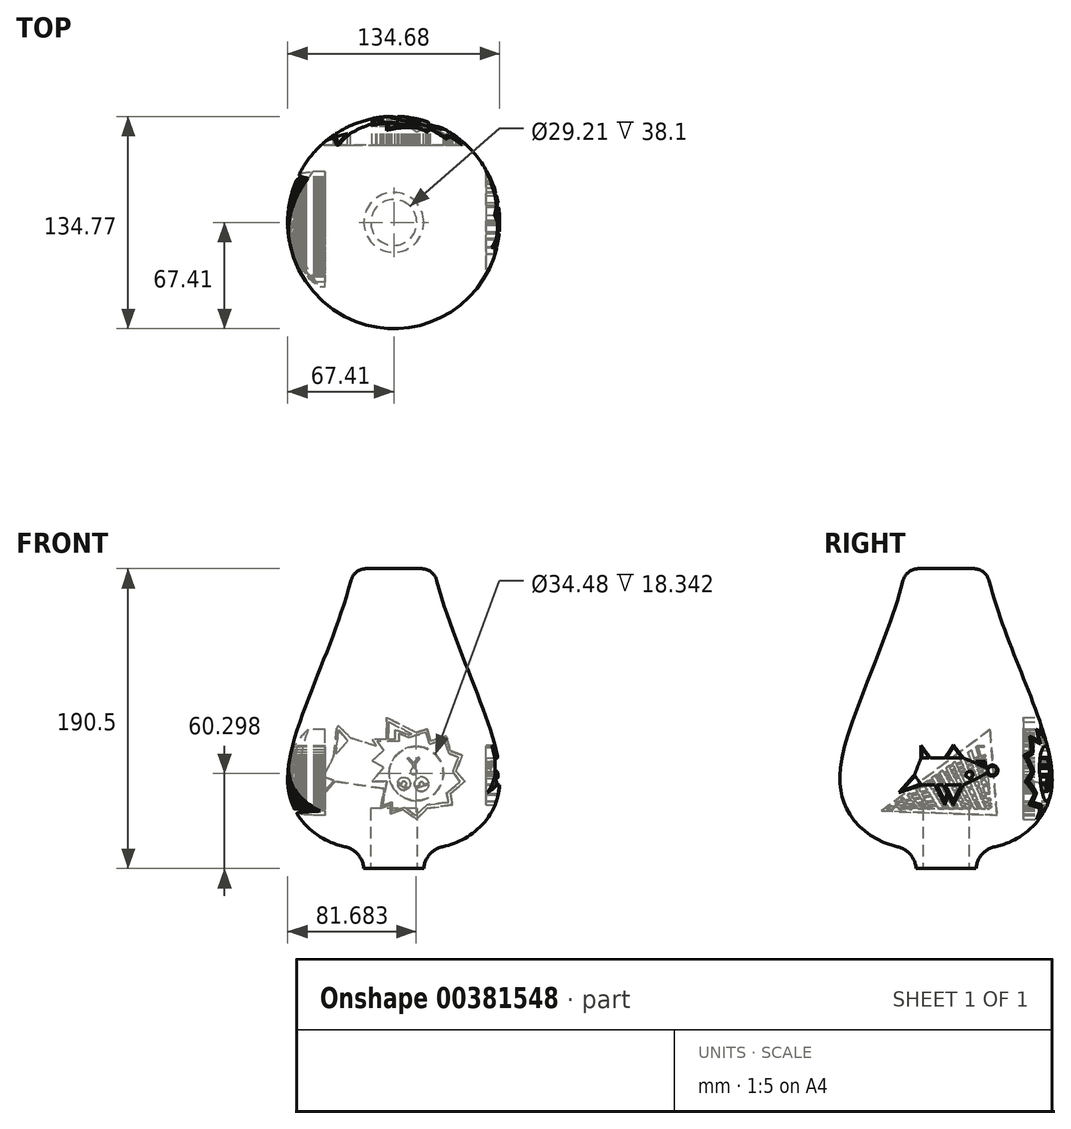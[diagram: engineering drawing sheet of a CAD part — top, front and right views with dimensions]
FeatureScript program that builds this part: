
annotation { "Feature Type Name" : "Feature", "Feature Type Description" : "" }
export const myFeature = defineFeature(function(context is Context, id is Id, definition is map)
    precondition{}
    {
        {
            var Q0;
            Q0=qCreatedBy(makeId("Right.planeOp"),FACE);
            var sketch = newSketch(context, id + "F0", { "sketchPlane" : qUnion([Q0])});
            skLineSegment(sketch, "E0", {"start": v(0, 38.68) * mm, "end": v(0, -139.12) * mm});
            skLineSegment(sketch, "E1", {"start": v(0, 38.68) * mm, "end": v(-25.4, 38.68) * mm});
            skFitSpline(sketch, "E2", {"points": [v(0, -139.12) * mm, v(-39.73, -135.25) * mm, v(-67.26, -98.84) * mm, v(-25.4, 38.68) * mm], "startDerivative": vector(-163.88, -7.65) * mm, "endDerivative": vector(75.35, 332.23) * mm});
            skLineSegment(sketch, "E3", {"start": v(0, -139.12) * mm, "end": v(-21.65, -139.3) * mm});
            skPoint(sketch, "E4.orphan", {"position": v(-79.02, -139.76) * mm});
            skSolve(sketch);
        }
        {
            var Q0;
            Q0=makeQuery(id+"F0.imprint","IMPRINT",FACE,{"disambiguationData":[TD([[makeQuery(id+"F0.imprint","IMPRINT",EDGE,{"derivedFrom":sQuery(id+"F0.wireOp",EDGE,"E0")}),-1.0]])]});
            var Q1;
            Q1=sQuery(id+"F0.wireOp",EDGE,"E0");
            revolve(context, id + "F1", {"entities" : qUnion([Q0]), "axis" : qUnion([Q1]), "revolveType" : RevolveType.FULL});
        }
        {
            var Q0;
            Q0=makeQuery(id+"F1.opRevolve","SWEPT_FACE",FACE,{"disambiguationData":[OSD([sQuery(id+"F0.wireOp",EDGE,"E1")])]});
            cPlane(context, id + "F2", {"entities" : qUnion([Q0]), "cplaneType" : CPlaneType.OFFSET, "offset" : 177.8 * mm, "oppositeDirection" : true, "width" : 152.4 * mm, "height" : 152.4 * mm});
        }
        {
            var Q0;
            Q0=qCreatedBy(id+"F2.planeOp",FACE);
            var sketch = newSketch(context, id + "F3", { "sketchPlane" : qUnion([Q0])});
            skCircle(sketch, "E5", {"center": v(0, 0) * mm, "radius": 19.05 * mm});
            skCircle(sketch, "E6", {"center": v(0, 0) * mm, "radius": 14.6 * mm});
            skSolve(sketch);
        }
        {
            var Q0;
            Q0=makeQuery(id+"F3.imprint","IMPRINT",FACE,{"disambiguationData":[TD([[makeQuery(id+"F3.imprint","IMPRINT",EDGE,{"derivedFrom":sQuery(id+"F3.wireOp",EDGE,"E6")}),1.0]])]});
            extrude(context, id + "F4", {"entities" : qUnion([Q0]), "operationType" : NewBodyOperationType.REMOVE, "depth" : 25.4 * mm, "hasSecondDirection" : true, "secondDirectionOppositeDirection" : true, "secondDirectionDepth" : 121.16 * mm});
        }
        {
            var Q0;
            Q0=qCreatedBy(makeId("Right.planeOp"),FACE);
            cPlane(context, id + "F5", {"entities" : qUnion([Q0]), "cplaneType" : CPlaneType.OFFSET, "offset" : 69.1 * mm, "width" : 152.4 * mm, "height" : 152.4 * mm});
        }
        {
            var Q0;
            Q0 = qSketchRegion(id + "F3", true);
            extrude(context, id + "F6", {"entities" : qUnion([Q0]), "operationType" : NewBodyOperationType.ADD, "oppositeDirection" : true, "depth" : 12.7 * mm});
        }
        {
            var Q0;
            Q0=makeQuery(id+"F6.boolean.opBoolean","INTERSECT",EDGE,{"derivedFrom":[makeQuery(id+"F1.opRevolve","SWEPT_FACE",FACE,{"disambiguationData":[OSD([sQuery(id+"F0.wireOp",EDGE,"E3")])]}),makeQuery(id+"F6.opExtrude","SWEPT_FACE",FACE,{"disambiguationData":[OSD([sQuery(id+"F3.wireOp",EDGE,"E5")])]})]});
            fillet(context, id + "F7", {"entities" : qUnion([Q0]), "radius" : 15.24 * mm, "tangentPropagation" : true, "allowEdgeOverflow" : false});
        }
        {
            var Q0;
            Q0=makeQuery(id+"F1.opRevolve","SWEPT_EDGE",EDGE,{"disambiguationData":[OSD([sQuery(id+"F0.wireOp",EDGE,"E1"),sQuery(id+"F0.wireOp",EDGE,"E2")])]});
            fillet(context, id + "F8", {"entities" : qUnion([Q0]), "radius" : 10.16 * mm, "tangentPropagation" : true, "allowEdgeOverflow" : false});
        }
        {
            var Q0;
            Q0=qCreatedBy(id+"F5.planeOp",FACE);
            var sketch = newSketch(context, id + "F9", { "sketchPlane" : qUnion([Q0])});
            skPoint(sketch, "E7.endSnap0", {"position": v(0.02, -69.9) * mm});
            skPoint(sketch, "E8.endSnap0", {"position": v(4.6, -119.36) * mm});
            skLineSegment(sketch, "E9", {"start": v(10.93, -98.82) * mm, "end": v(4.58, -111.52) * mm});
            skLineSegment(sketch, "E10", {"start": v(4.58, -111.52) * mm, "end": v(1.4, -105.17) * mm});
            skLineSegment(sketch, "E11", {"start": v(-15.48, -98.82) * mm, "end": v(-7.06, -98.82) * mm});
            skLineSegment(sketch, "E12", {"start": v(10.93, -98.82) * mm, "end": v(26.8, -90.88) * mm});
            skLineSegment(sketch, "E13", {"start": v(26.75, -88.46) * mm, "end": v(22.07, -86.39) * mm});
            skLineSegment(sketch, "E14", {"start": v(10.93, -81.45) * mm, "end": v(4.58, -73.28) * mm});
            skLineSegment(sketch, "E15", {"start": v(4.58, -73.28) * mm, "end": v(-0.66, -81.45) * mm});
            skLineSegment(sketch, "E16", {"start": v(-0.66, -81.45) * mm, "end": v(-10.09, -81.45) * mm});
            skLineSegment(sketch, "E17", {"start": v(-10.09, -81.45) * mm, "end": v(-15.9, -73.59) * mm});
            skLineSegment(sketch, "E18", {"start": v(-15.9, -73.59) * mm, "end": v(-15.9, -81.45) * mm});
            skArc(sketch, "E19", {"start": v(26.8, -90.88) * mm, "mid": v(32.19, -89.55) * mm, "end": v(26.75, -88.46) * mm});
            skPoint(sketch, "E20.start.orphan", {"position": v(-9.13, -111.52) * mm});
            skLineSegment(sketch, "E21", {"start": v(1.4, -105.17) * mm, "end": v(-0.82, -111.3) * mm});
            skLineSegment(sketch, "E22", {"start": v(-0.82, -111.3) * mm, "end": v(-7.06, -98.82) * mm});
            skLineSegment(sketch, "E23", {"start": v(-15.9, -81.45) * mm, "end": v(-20.1, -92.38) * mm});
            skLineSegment(sketch, "E24", {"start": v(-20.1, -92.38) * mm, "end": v(-29.9, -103.5) * mm});
            skLineSegment(sketch, "E25", {"start": v(-29.9, -103.5) * mm, "end": v(-15.48, -98.82) * mm});
            skCircle(sketch, "E26", {"center": v(14.89, -92.23) * mm, "radius": 2.23 * mm});
            skLineSegment(sketch, "E27", {"start": v(24.42, -87.42) * mm, "end": v(24.42, -84.23) * mm});
            skLineSegment(sketch, "E28", {"start": v(24.42, -84.23) * mm, "end": v(22.07, -84.23) * mm});
            skLineSegment(sketch, "E29", {"start": v(21.78, -84.23) * mm, "end": v(21.78, -86.25) * mm});
            skLineSegment(sketch, "E30", {"start": v(21.78, -84.23) * mm, "end": v(19.44, -84.23) * mm});
            skLineSegment(sketch, "E31", {"start": v(19.44, -84.23) * mm, "end": v(19.44, -85.22) * mm});
            skCircle(sketch, "E32", {"center": v(29.35, -89.61) * mm, "radius": 2.84 * mm});
            skLineSegment(sketch, "E33", {"start": v(25.01, -87.69) * mm, "end": v(25.01, -83.8) * mm});
            skLineSegment(sketch, "E34", {"start": v(25.01, -83.8) * mm, "end": v(18.9, -83.8) * mm});
            skLineSegment(sketch, "E35", {"start": v(18.9, -83.8) * mm, "end": v(18.9, -84.97) * mm});
            skArc(sketch, "E36", {"start": v(26.2, -91.19) * mm, "mid": v(32.88, -89.53) * mm, "end": v(26.12, -88.18) * mm});
            skLineSegment(sketch, "E37", {"start": v(22.07, -84.23) * mm, "end": v(22.07, -86.39) * mm});
            skLineSegment(sketch, "E38.trimOffspring", {"start": v(21.78, -86.25) * mm, "end": v(10.93, -81.45) * mm});
            skLineSegment(sketch, "E39", {"start": v(9.83, -98.82) * mm, "end": v(-0.82, -98.82) * mm});
            skLineSegment(sketch, "E40", {"start": v(9.83, -98.82) * mm, "end": v(4.58, -109.32) * mm});
            skLineSegment(sketch, "E41", {"start": v(4.58, -109.32) * mm, "end": v(-0.82, -98.82) * mm});
            skLineSegment(sketch, "E42", {"start": v(-5.86, -98.82) * mm, "end": v(-0.82, -108.9) * mm});
            skLineSegment(sketch, "E43", {"start": v(-0.82, -108.9) * mm, "end": v(0.9, -104.16) * mm});
            skLineSegment(sketch, "E44.trimOffspring", {"start": v(0.9, -104.16) * mm, "end": v(-1.77, -98.82) * mm});
            skLineSegment(sketch, "E45.trimOffspring", {"start": v(-1.77, -98.82) * mm, "end": v(-5.86, -98.82) * mm});
            skLineSegment(sketch, "E46", {"start": v(10.27, -81.45) * mm, "end": v(4.58, -81.45) * mm});
            skLineSegment(sketch, "E47", {"start": v(10.27, -81.45) * mm, "end": v(4.58, -74.19) * mm});
            skPoint(sketch, "E48.end.orphan", {"position": v(4.58, -81.45) * mm});
            skLineSegment(sketch, "E49", {"start": v(-10.85, -81.45) * mm, "end": v(-15.45, -81.45) * mm});
            skLineSegment(sketch, "E50", {"start": v(-10.85, -81.45) * mm, "end": v(-15.45, -74.88) * mm});
            skLineSegment(sketch, "E51", {"start": v(-15.45, -74.88) * mm, "end": v(-15.45, -81.45) * mm});
            skLineSegment(sketch, "E52", {"start": v(10.27, -81.45) * mm, "end": v(-0.08, -81.45) * mm});
            skLineSegment(sketch, "E53", {"start": v(4.58, -74.19) * mm, "end": v(-0.08, -81.45) * mm});
            skPoint(sketch, "E54.orphan", {"position": v(-0.22, -81.45) * mm});
            skLineSegment(sketch, "E55", {"start": v(-15.92, -98.2) * mm, "end": v(-19.67, -92.97) * mm});
            skLineSegment(sketch, "E56", {"start": v(-17.79, -95.6) * mm, "end": v(-15.92, -98.2) * mm});
            skLineSegment(sketch, "E57", {"start": v(-15.92, -98.2) * mm, "end": v(-28.98, -102.9) * mm});
            skLineSegment(sketch, "E58", {"start": v(-28.98, -102.9) * mm, "end": v(-19.67, -92.97) * mm});
            skSolve(sketch);
        }
        {
            var Q0;
            {var subQ7=sQuery(id+"F9.wireOp",EDGE,"E9");Q0=makeQuery(id+"F9.imprint","IMPRINT",FACE,{"disambiguationData":[TD([[makeQuery(id+"F9.imprint","IMPRINT",EDGE,{"derivedFrom":subQ7}),-1.0]])]});}
            var Q1;
            {var subQ3=sQuery(id+"F9.wireOp",EDGE,"E36");Q1=makeQuery(id+"F9.imprint","IMPRINT",FACE,{"disambiguationData":[TD([[makeQuery(id+"F9.imprint","IMPRINT",EDGE,{"derivedFrom":subQ3}),1.0]])]});}
            var Q2;
            {var subQ0=sQuery(id+"F9.wireOp",EDGE,"E27");Q2=makeQuery(id+"F9.imprint","IMPRINT",FACE,{"disambiguationData":[TD([[makeQuery(id+"F9.imprint","IMPRINT",EDGE,{"derivedFrom":subQ0}),-1.0]])]});}
            extrude(context, id + "F10", {"entities" : qUnion([Q0, Q1, Q2]), "operationType" : NewBodyOperationType.REMOVE, "oppositeDirection" : true, "depth" : 10.67 * mm});
        }
        {
            var Q0;
            Q0=qCreatedBy(makeId("Front.planeOp"),FACE);
            cPlane(context, id + "F11", {"entities" : qUnion([Q0]), "cplaneType" : CPlaneType.OFFSET, "offset" : 69.1 * mm, "oppositeDirection" : true, "width" : 152.4 * mm, "height" : 152.4 * mm});
        }
        {
            var Q0;
            Q0=qCreatedBy(id+"F11.planeOp",FACE);
            var sketch = newSketch(context, id + "F12", { "sketchPlane" : qUnion([Q0])});
            skCircle(sketch, "E59", {"center": v(14.27, -91.52) * mm, "radius": 17.24 * mm});
            skLineSegment(sketch, "E60", {"start": v(5.73, -114.4) * mm, "end": v(14.47, -120.5) * mm});
            skLineSegment(sketch, "E61", {"start": v(14.47, -120.5) * mm, "end": v(21.2, -113.75) * mm});
            skLineSegment(sketch, "E62", {"start": v(21.2, -113.75) * mm, "end": v(37.14, -111.33) * mm});
            skLineSegment(sketch, "E63", {"start": v(37.14, -111.33) * mm, "end": v(36.07, -104.25) * mm});
            skLineSegment(sketch, "E64", {"start": v(36.07, -104.25) * mm, "end": v(45.1, -96.63) * mm});
            skLineSegment(sketch, "E65", {"start": v(45.1, -96.63) * mm, "end": v(39.67, -90.18) * mm});
            skLineSegment(sketch, "E66", {"start": v(39.67, -90.18) * mm, "end": v(43.4, -79.8) * mm});
            skLineSegment(sketch, "E67", {"start": v(43.4, -79.8) * mm, "end": v(36.07, -77.17) * mm});
            skLineSegment(sketch, "E68", {"start": v(36.07, -77.17) * mm, "end": v(33.2, -67.7) * mm});
            skLineSegment(sketch, "E69", {"start": v(33.2, -67.7) * mm, "end": v(23.43, -70.65) * mm});
            skLineSegment(sketch, "E70", {"start": v(23.43, -70.65) * mm, "end": v(21.2, -63.27) * mm});
            skLineSegment(sketch, "E71", {"start": v(21.2, -63.27) * mm, "end": v(9.36, -66.85) * mm});
            skLineSegment(sketch, "E72", {"start": v(9.36, -66.85) * mm, "end": v(0.81, -63.67) * mm});
            skLineSegment(sketch, "E73", {"start": v(0.81, -63.67) * mm, "end": v(0.81, -69.85) * mm});
            skLineSegment(sketch, "E74", {"start": v(0.81, -69.85) * mm, "end": v(-13.66, -69.85) * mm});
            skLineSegment(sketch, "E75", {"start": v(-13.66, -69.85) * mm, "end": v(-9.34, -77.17) * mm});
            skLineSegment(sketch, "E76", {"start": v(-9.34, -77.17) * mm, "end": v(-15.86, -84.2) * mm});
            skLineSegment(sketch, "E77", {"start": v(-15.86, -84.2) * mm, "end": v(-8.42, -88.08) * mm});
            skLineSegment(sketch, "E78", {"start": v(-8.42, -88.08) * mm, "end": v(-15.86, -97.7) * mm});
            skLineSegment(sketch, "E79", {"start": v(-15.86, -97.7) * mm, "end": v(-5.5, -97.7) * mm});
            skLineSegment(sketch, "E80", {"start": v(-5.5, -97.7) * mm, "end": v(-8.42, -113.75) * mm});
            skLineSegment(sketch, "E81", {"start": v(-8.42, -113.75) * mm, "end": v(-1.93, -111.33) * mm});
            skLineSegment(sketch, "E82", {"start": v(-1.93, -111.33) * mm, "end": v(-1.93, -117.16) * mm});
            skLineSegment(sketch, "E83", {"start": v(-1.93, -117.16) * mm, "end": v(5.73, -114.4) * mm});
            skCircle(sketch, "E84", {"center": v(6.45, -97.92) * mm, "radius": 4.15 * mm});
            skPoint(sketch, "E84.centerSnap0", {"position": v(-3.87, -97.92) * mm});
            skCircle(sketch, "E85", {"center": v(17.63, -98.23) * mm, "radius": 4.55 * mm});
            skLineSegment(sketch, "E86", {"start": v(12.23, -88.13) * mm, "end": v(12.23, -86.17) * mm});
            skLineSegment(sketch, "E87", {"start": v(12.23, -84.52) * mm, "end": v(13.07, -84.52) * mm});
            skLineSegment(sketch, "E88", {"start": v(13.07, -85.85) * mm, "end": v(13.07, -88.16) * mm});
            skLineSegment(sketch, "E89", {"start": v(12.23, -84.52) * mm, "end": v(9.5, -81.32) * mm});
            skLineSegment(sketch, "E90", {"start": v(9.5, -81.32) * mm, "end": v(8.7, -82.01) * mm});
            skLineSegment(sketch, "E91", {"start": v(8.7, -82.01) * mm, "end": v(12.23, -86.17) * mm});
            skLineSegment(sketch, "E92", {"start": v(13.07, -84.52) * mm, "end": v(15.75, -81.21) * mm});
            skLineSegment(sketch, "E93", {"start": v(15.75, -81.21) * mm, "end": v(16.4, -81.74) * mm});
            skLineSegment(sketch, "E94", {"start": v(16.4, -81.74) * mm, "end": v(13.07, -85.85) * mm});
            skCircle(sketch, "E95", {"center": v(12.6, -90.1) * mm, "radius": 2 * mm});
            skPoint(sketch, "E96.end.orphan", {"position": v(12.23, -91.52) * mm});
            skPoint(sketch, "E96.start.orphan", {"position": v(13.07, -91.52) * mm});
            skLineSegment(sketch, "E97", {"start": v(2.42, -96.93) * mm, "end": v(9.4, -100.84) * mm});
            skLineSegment(sketch, "E98", {"start": v(2.3, -97.77) * mm, "end": v(8.52, -101.52) * mm});
            skLineSegment(sketch, "E99", {"start": v(13.42, -99.94) * mm, "end": v(22.14, -97.67) * mm});
            skLineSegment(sketch, "E100", {"start": v(13.9, -100.82) * mm, "end": v(22.17, -98.35) * mm});
            skArc(sketch, "E101", {"start": v(6.83, -99.4) * mm, "mid": v(7.2, -96.6) * mm, "end": v(5, -98.37) * mm});
            skArc(sketch, "E102", {"start": v(19.02, -98.49) * mm, "mid": v(17.27, -96.86) * mm, "end": v(16.54, -99.13) * mm});
            skPoint(sketch, "E103.start.orphan", {"position": v(-5.5, -74.64) * mm});
            skPoint(sketch, "E104.end.orphan", {"position": v(-9.08, -84.2) * mm});
            skPoint(sketch, "E105.end.orphan", {"position": v(-5.93, -90.18) * mm});
            skPoint(sketch, "E106.end.orphan", {"position": v(-8.42, -94.97) * mm});
            skPoint(sketch, "E107.orphan", {"position": v(-4.16, -100.29) * mm});
            skPoint(sketch, "E108.end.orphan", {"position": v(-3.59, -95.56) * mm});
            skPoint(sketch, "E109.end.orphan", {"position": v(-5.5, -111.33) * mm});
            skPoint(sketch, "E110.start.orphan", {"position": v(1.76, -111.33) * mm});
            skPoint(sketch, "E111.end.orphan", {"position": v(8.57, -111.33) * mm});
            skPoint(sketch, "E112.end.orphan", {"position": v(14.47, -114.4) * mm});
            skPoint(sketch, "E113.end.orphan", {"position": v(21.2, -111.33) * mm});
            skPoint(sketch, "E114.end.orphan", {"position": v(32.75, -100.29) * mm});
            skPoint(sketch, "E115.end.orphan", {"position": v(39.67, -94.46) * mm});
            skPoint(sketch, "E116.end.orphan", {"position": v(36.07, -90.18) * mm});
            skPoint(sketch, "E117.end.orphan", {"position": v(37.14, -80.63) * mm});
            skPoint(sketch, "E118.start.orphan", {"position": v(1.76, -74.64) * mm});
            skPoint(sketch, "E119.end.orphan", {"position": v(17.63, -69.2) * mm});
            skPoint(sketch, "E120.start.orphan", {"position": v(21.2, -73.44) * mm});
            skPoint(sketch, "E121.end.orphan", {"position": v(30.49, -77.17) * mm});
            skPoint(sketch, "E122.end.orphan", {"position": v(9.36, -71.68) * mm});
            skPoint(sketch, "E122.start.orphan", {"position": v(4.59, -69.2) * mm});
            skLineSegment(sketch, "E123", {"start": v(7.2, -113.1) * mm, "end": v(13.9, -118.2) * mm});
            skLineSegment(sketch, "E124", {"start": v(13.9, -118.2) * mm, "end": v(21.2, -111.33) * mm});
            skLineSegment(sketch, "E125", {"start": v(21.2, -111.33) * mm, "end": v(34.6, -109.85) * mm});
            skLineSegment(sketch, "E126", {"start": v(34.6, -109.85) * mm, "end": v(33.63, -103.63) * mm});
            skLineSegment(sketch, "E127", {"start": v(33.63, -103.63) * mm, "end": v(42.17, -96.75) * mm});
            skLineSegment(sketch, "E128", {"start": v(42.17, -96.75) * mm, "end": v(37.55, -90.17) * mm});
            skLineSegment(sketch, "E129", {"start": v(37.55, -90.17) * mm, "end": v(40.92, -81.01) * mm});
            skLineSegment(sketch, "E130", {"start": v(40.92, -81.01) * mm, "end": v(35, -78.83) * mm});
            skLineSegment(sketch, "E131", {"start": v(35, -78.83) * mm, "end": v(32.03, -70.1) * mm});
            skLineSegment(sketch, "E132", {"start": v(32.03, -70.1) * mm, "end": v(22.54, -72.78) * mm});
            skLineSegment(sketch, "E133", {"start": v(22.54, -72.78) * mm, "end": v(20.44, -65.36) * mm});
            skLineSegment(sketch, "E134", {"start": v(20.44, -65.36) * mm, "end": v(9.4, -68.48) * mm});
            skLineSegment(sketch, "E135", {"start": v(9.4, -68.48) * mm, "end": v(3.34, -66.04) * mm});
            skLineSegment(sketch, "E136", {"start": v(3.34, -66.04) * mm, "end": v(3.34, -70.97) * mm});
            skLineSegment(sketch, "E137", {"start": v(3.34, -70.97) * mm, "end": v(-10.6, -70.97) * mm});
            skLineSegment(sketch, "E138", {"start": v(-10.6, -70.97) * mm, "end": v(-6.35, -76.81) * mm});
            skLineSegment(sketch, "E139", {"start": v(-6.35, -76.81) * mm, "end": v(-13.81, -83.47) * mm});
            skLineSegment(sketch, "E140", {"start": v(-13.81, -83.47) * mm, "end": v(-6.4, -87.46) * mm});
            skLineSegment(sketch, "E141", {"start": v(-6.4, -87.46) * mm, "end": v(-13.81, -96.5) * mm});
            skLineSegment(sketch, "E142", {"start": v(-13.81, -96.5) * mm, "end": v(-4.44, -96.5) * mm});
            skLineSegment(sketch, "E143", {"start": v(-4.44, -96.5) * mm, "end": v(-7.12, -111.92) * mm});
            skLineSegment(sketch, "E144", {"start": v(-7.12, -111.92) * mm, "end": v(-1.1, -109.64) * mm});
            skLineSegment(sketch, "E145", {"start": v(-1.1, -109.64) * mm, "end": v(-1.1, -115.36) * mm});
            skLineSegment(sketch, "E146", {"start": v(-1.1, -115.36) * mm, "end": v(7.2, -113.1) * mm});
            skLineSegment(sketch, "E147", {"start": v(-6.1, -101.03) * mm, "end": v(-37.05, -96.5) * mm});
            skPoint(sketch, "E147.endSnap0", {"position": v(-9.13, -96.5) * mm});
            skLineSegment(sketch, "E148", {"start": v(-44.57, -93.6) * mm, "end": v(-38.23, -80.61) * mm});
            skLineSegment(sketch, "E149", {"start": v(-38.23, -80.61) * mm, "end": v(-36.03, -60) * mm});
            skLineSegment(sketch, "E150", {"start": v(-36.03, -60) * mm, "end": v(-27.41, -68.9) * mm});
            skLineSegment(sketch, "E151", {"start": v(-27.41, -68.9) * mm, "end": v(-11.2, -74.03) * mm});
            skLineSegment(sketch, "E152", {"start": v(-4.64, -69.85) * mm, "end": v(-4.64, -55.72) * mm});
            skLineSegment(sketch, "E153", {"start": v(-4.64, -55.72) * mm, "end": v(14.03, -65.44) * mm});
            skPoint(sketch, "E154.orphan", {"position": v(-40.81, -95.05) * mm});
            skLineSegment(sketch, "E155", {"start": v(-36.84, -79.1) * mm, "end": v(-29.23, -70.86) * mm});
            skLineSegment(sketch, "E156", {"start": v(-36.84, -79.1) * mm, "end": v(-35.2, -63.81) * mm});
            skLineSegment(sketch, "E157", {"start": v(-35.2, -63.81) * mm, "end": v(-29.23, -70.86) * mm});
            skPoint(sketch, "E158.orphan", {"position": v(-32.82, -74.76) * mm});
            skLineSegment(sketch, "E159", {"start": v(-3.35, -69.85) * mm, "end": v(-3.35, -58.61) * mm});
            skLineSegment(sketch, "E160", {"start": v(-3.35, -58.61) * mm, "end": v(11.25, -66.28) * mm});
            skLineSegment(sketch, "E161", {"start": v(-44.57, -93.6) * mm, "end": v(-44.57, -104.75) * mm});
            skLineSegment(sketch, "E162", {"start": v(-44.57, -104.75) * mm, "end": v(-37.05, -96.5) * mm});
            skLineSegment(sketch, "E163", {"start": v(-43.88, -93.6) * mm, "end": v(-44, -102.63) * mm});
            skLineSegment(sketch, "E164", {"start": v(-44, -102.63) * mm, "end": v(-38.02, -95.96) * mm});
            skLineSegment(sketch, "E165", {"start": v(-38.02, -95.96) * mm, "end": v(-43.88, -93.6) * mm});
            skSolve(sketch);
        }
        {
            var Q0;
            {var subQ1=sQuery(id+"F12.wireOp",EDGE,"74fbe37b-10bf-4360-813b-6cc7bf69f318");Q0=makeQuery(id+"F12.imprint","IMPRINT",FACE,{"disambiguationData":[TD([[makeQuery(id+"F12.imprint","IMPRINT",EDGE,{"derivedFrom":subQ1}),-1.0]])]});}
            var Q1;
            {var subQ3=sQuery(id+"F12.wireOp",EDGE,"20278019-62cc-441b-9a75-802a49bbc266");Q1=makeQuery(id+"F12.imprint","IMPRINT",FACE,{"disambiguationData":[TD([[makeQuery(id+"F12.imprint","IMPRINT",EDGE,{"derivedFrom":subQ3}),-1.0]])]});}
            var Q2;
            {var subQ0=sQuery(id+"F12.wireOp",EDGE,"f76c5c3a-d76c-4985-a438-fa1affc6520c");Q2=makeQuery(id+"F12.imprint","IMPRINT",FACE,{"disambiguationData":[TD([[makeQuery(id+"F12.imprint","IMPRINT",EDGE,{"derivedFrom":subQ0}),1.0]])]});}
            var Q3;
            {var subQ0=sQuery(id+"F12.wireOp",EDGE,"a305504d-e68e-4a7d-bf96-f3220a1708c9");Q3=makeQuery(id+"F12.imprint","IMPRINT",FACE,{"disambiguationData":[TD([[makeQuery(id+"F12.imprint","IMPRINT",EDGE,{"derivedFrom":subQ0}),1.0]])]});}
            var Q4;
            {var subQ7=sQuery(id+"F12.wireOp",EDGE,"b3788da2-0d39-4c1d-bc5e-2863974d03fb");Q4=makeQuery(id+"F12.imprint","IMPRINT",FACE,{"disambiguationData":[TD([[makeQuery(id+"F12.imprint","IMPRINT",EDGE,{"derivedFrom":subQ7}),1.0]])]});}
            var Q5;
            {var subQ6=sQuery(id+"F12.wireOp",EDGE,"7fed4fa2-91c2-4125-8361-faa614cffb4f");Q5=makeQuery(id+"F12.imprint","IMPRINT",FACE,{"disambiguationData":[TD([[makeQuery(id+"F12.imprint","IMPRINT",EDGE,{"derivedFrom":subQ6}),1.0]])]});}
            var Q6;
            Q6=makeQuery(id+"F12.imprint","IMPRINT",FACE,{"disambiguationData":[TD([[makeQuery(id+"F12.imprint","IMPRINT",EDGE,{"derivedFrom":sQuery(id+"F12.wireOp",EDGE,"fd0f0aac-86a8-40e2-b083-f11eedc4afae")}),1.0]])]});
            var Q7;
            Q7=makeQuery(id+"F12.imprint","IMPRINT",FACE,{"disambiguationData":[TD([[makeQuery(id+"F12.imprint","IMPRINT",EDGE,{"derivedFrom":sQuery(id+"F12.wireOp",EDGE,"afd5d1f2-45d2-46e9-bd26-ee5be468e809")}),1.0]])]});
            var Q8;
            Q8=makeQuery(id+"F12.imprint","IMPRINT",FACE,{"disambiguationData":[TD([[makeQuery(id+"F12.imprint","IMPRINT",EDGE,{"derivedFrom":sQuery(id+"F12.wireOp",EDGE,"E60")}),1.0]])]});
            var Q9;
            {var subQ3=sQuery(id+"F12.wireOp",EDGE,"E76");Q9=makeQuery(id+"F12.imprint","IMPRINT",FACE,{"disambiguationData":[TD([[makeQuery(id+"F12.imprint","IMPRINT",EDGE,{"derivedFrom":subQ3}),-1.0]])]});}
            var Q10;
            {var subQ3=sQuery(id+"F12.wireOp",EDGE,"E152");Q10=makeQuery(id+"F12.imprint","IMPRINT",FACE,{"disambiguationData":[TD([[makeQuery(id+"F12.imprint","IMPRINT",EDGE,{"derivedFrom":subQ3}),-1.0]])]});}
            var Q11;
            Q11=makeQuery(id+"F12.imprint","IMPRINT",FACE,{"disambiguationData":[TD([[makeQuery(id+"F12.imprint","IMPRINT",EDGE,{"derivedFrom":sQuery(id+"F12.wireOp",EDGE,"E59")}),1.0]])]});
            var Q12;
            {var subQ0=sQuery(id+"F12.wireOp",EDGE,"E101");Q12=makeQuery(id+"F12.imprint","IMPRINT",FACE,{"disambiguationData":[TD([[makeQuery(id+"F12.imprint","IMPRINT",EDGE,{"derivedFrom":subQ0}),1.0]])]});}
            var Q13;
            {var subQ0=sQuery(id+"F12.wireOp",EDGE,"E101");Q13=makeQuery(id+"F12.imprint","IMPRINT",FACE,{"disambiguationData":[TD([[makeQuery(id+"F12.imprint","IMPRINT",EDGE,{"derivedFrom":subQ0}),1.0]])]});}
            var Q14;
            {var subQ0=sQuery(id+"F12.wireOp",EDGE,"E102");Q14=makeQuery(id+"F12.imprint","IMPRINT",FACE,{"disambiguationData":[TD([[makeQuery(id+"F12.imprint","IMPRINT",EDGE,{"derivedFrom":subQ0}),1.0]])]});}
            var Q15;
            {var subQ7=sQuery(id+"F12.wireOp",EDGE,"E100");Q15=makeQuery(id+"F12.imprint","IMPRINT",FACE,{"disambiguationData":[TD([[makeQuery(id+"F12.imprint","IMPRINT",EDGE,{"derivedFrom":subQ7}),1.0]])]});}
            var Q16;
            {var subQ6=sQuery(id+"F12.wireOp",EDGE,"E98");Q16=makeQuery(id+"F12.imprint","IMPRINT",FACE,{"disambiguationData":[TD([[makeQuery(id+"F12.imprint","IMPRINT",EDGE,{"derivedFrom":subQ6}),1.0]])]});}
            extrude(context, id + "F13", {"entities" : qUnion([Q0, Q1, Q2, Q3, Q4, Q5, Q6, Q7, Q8, Q9, Q10, Q11, Q12, Q13, Q14, Q15, Q16]), "operationType" : NewBodyOperationType.REMOVE, "depth" : 20.07 * mm});
        }
        {
            var Q0;
            Q0=qCreatedBy(makeId("Right.planeOp"),FACE);
            cPlane(context, id + "F14", {"entities" : qUnion([Q0]), "cplaneType" : CPlaneType.OFFSET, "offset" : 69.1 * mm, "oppositeDirection" : true, "width" : 152.4 * mm, "height" : 152.4 * mm});
        }
        {
            var Q0;
            Q0=qCreatedBy(id+"F14.planeOp",FACE);
            var sketch = newSketch(context, id + "F15", { "sketchPlane" : qUnion([Q0])});
            skLineSegment(sketch, "E166", {"start": v(-41.2, -115.33) * mm, "end": v(27.92, -63.43) * mm});
            skLineSegment(sketch, "E167", {"start": v(-41.2, -115.33) * mm, "end": v(32.3, -117.94) * mm});
            skLineSegment(sketch, "E168", {"start": v(32.3, -117.94) * mm, "end": v(27.92, -63.43) * mm});
            skLineSegment(sketch, "E169", {"start": v(-37.9, -114.19) * mm, "end": v(23.85, -71.23) * mm});
            skLineSegment(sketch, "E170", {"start": v(23.85, -71.23) * mm, "end": v(29, -113.85) * mm});
            skLineSegment(sketch, "E171", {"start": v(29, -113.85) * mm, "end": v(-37.9, -114.19) * mm});
            skPoint(sketch, "E172.end.orphan", {"position": v(30.1, -90.69) * mm});
            skLineSegment(sketch, "E173", {"start": v(-29.63, -114.15) * mm, "end": v(-30.6, -112.76) * mm});
            skLineSegment(sketch, "E174", {"start": v(-32.3, -110.3) * mm, "end": v(-31.15, -109.5) * mm});
            skLineSegment(sketch, "E175", {"start": v(-30.79, -110.02) * mm, "end": v(-29.55, -111.8) * mm});
            skLineSegment(sketch, "E176", {"start": v(-23.4, -114.12) * mm, "end": v(-23.7, -113.73) * mm});
            skLineSegment(sketch, "E177", {"start": v(-27.35, -106.85) * mm, "end": v(-26.07, -108.49) * mm});
            skLineSegment(sketch, "E178", {"start": v(-17.29, -114.08) * mm, "end": v(-18.03, -113.17) * mm});
            skLineSegment(sketch, "E179", {"start": v(-23.42, -104.12) * mm, "end": v(-23.02, -104.62) * mm});
            skLineSegment(sketch, "E180", {"start": v(-19.23, -101.2) * mm, "end": v(-17.92, -103.52) * mm});
            skLineSegment(sketch, "E181", {"start": v(-17.34, -100.73) * mm, "end": v(-16.1, -103.13) * mm});
            skLineSegment(sketch, "E182", {"start": v(-4.45, -114.02) * mm, "end": v(-5.71, -111.97) * mm});
            skLineSegment(sketch, "E183", {"start": v(-11.68, -97.12) * mm, "end": v(-10.91, -98.35) * mm});
            skLineSegment(sketch, "E184", {"start": v(-8.95, -94.05) * mm, "end": v(-8.33, -95.2) * mm});
            skLineSegment(sketch, "E185", {"start": v(4.9, -113.97) * mm, "end": v(4.6, -113.43) * mm});
            skLineSegment(sketch, "E186", {"start": v(-4.2, -90.74) * mm, "end": v(-3.72, -91.63) * mm});
            skLineSegment(sketch, "E187", {"start": v(10.93, -113.94) * mm, "end": v(10.36, -112.87) * mm});
            skLineSegment(sketch, "E188", {"start": v(0, -87.82) * mm, "end": v(1.16, -90.04) * mm});
            skLineSegment(sketch, "E189", {"start": v(15.39, -113.92) * mm, "end": v(14.65, -112.45) * mm});
            skLineSegment(sketch, "E190", {"start": v(4.11, -84.96) * mm, "end": v(4.52, -85.81) * mm});
            skLineSegment(sketch, "E191", {"start": v(19.78, -113.18) * mm, "end": v(19.2, -112) * mm});
            skLineSegment(sketch, "E192", {"start": v(8.8, -81.7) * mm, "end": v(9.86, -84.2) * mm});
            skLineSegment(sketch, "E193", {"start": v(25.14, -113.87) * mm, "end": v(24.9, -113.32) * mm});
            skLineSegment(sketch, "E194", {"start": v(26.25, -113.86) * mm, "end": v(26.02, -113.18) * mm});
            skLineSegment(sketch, "E195", {"start": v(16.14, -76.6) * mm, "end": v(17.75, -81.8) * mm});
            skLineSegment(sketch, "E196", {"start": v(20.24, -74.6) * mm, "end": v(22.16, -80.46) * mm});
            skLineSegment(sketch, "E197", {"start": v(-34.74, -114.17) * mm, "end": v(-35.76, -112.7) * mm});
            skLineSegment(sketch, "E198", {"start": v(-34.84, -112.06) * mm, "end": v(-34.52, -112.52) * mm});
            skLineSegment(sketch, "E199", {"start": v(-27.92, -114.14) * mm, "end": v(-23.7, -113.73) * mm});
            skLineSegment(sketch, "E200", {"start": v(-1.24, -114) * mm, "end": v(1.78, -113.7) * mm});
            skLineSegment(sketch, "E201", {"start": v(20.12, -113.9) * mm, "end": v(22.34, -113.63) * mm});
            skLineSegment(sketch, "E202", {"start": v(-34.52, -112.52) * mm, "end": v(-31.1, -112.03) * mm});
            skLineSegment(sketch, "E203", {"start": v(-34, -113.26) * mm, "end": v(-30.6, -112.76) * mm});
            skLineSegment(sketch, "E204", {"start": v(-30.79, -110.02) * mm, "end": v(-27.18, -109.36) * mm});
            skLineSegment(sketch, "E205", {"start": v(-31.15, -109.5) * mm, "end": v(-27.63, -108.8) * mm});
            skPoint(sketch, "E206.endSnap0", {"position": v(21.9, -95.23) * mm});
            skLineSegment(sketch, "E207", {"start": v(-23.02, -104.62) * mm, "end": v(-17.92, -103.52) * mm});
            skLineSegment(sketch, "E208", {"start": v(-17.34, -100.73) * mm, "end": v(-13.28, -99.72) * mm});
            skLineSegment(sketch, "E209", {"start": v(-17.66, -100.11) * mm, "end": v(-13.68, -99.08) * mm});
            skLineSegment(sketch, "E210", {"start": v(-11.68, -97.12) * mm, "end": v(-7.84, -96.08) * mm});
            skLineSegment(sketch, "E211", {"start": v(-12.18, -96.3) * mm, "end": v(-8.33, -95.2) * mm});
            skLineSegment(sketch, "E212", {"start": v(-6.66, -93.35) * mm, "end": v(-3.35, -92.32) * mm});
            skLineSegment(sketch, "E213", {"start": v(-7.02, -92.71) * mm, "end": v(-3.72, -91.63) * mm});
            skLineSegment(sketch, "E214", {"start": v(1.64, -86.68) * mm, "end": v(4.52, -85.81) * mm});
            skLineSegment(sketch, "E215", {"start": v(20.24, -74.6) * mm, "end": v(24.26, -74.6) * mm});
            skLineSegment(sketch, "E216", {"start": v(20, -73.9) * mm, "end": v(24.17, -73.9) * mm});
            skPoint(sketch, "E217.orphan", {"position": v(-35.25, -113.44) * mm});
            skLineSegment(sketch, "E218.trimOffspring", {"start": v(-34, -113.26) * mm, "end": v(-33.38, -114.17) * mm});
            skLineSegment(sketch, "E219.trimOffspring", {"start": v(-31.1, -112.03) * mm, "end": v(-32.3, -110.3) * mm});
            skLineSegment(sketch, "E220.trimOffspring", {"start": v(-29.04, -112.54) * mm, "end": v(-28.3, -113.6) * mm});
            skLineSegment(sketch, "E221.trimOffspring", {"start": v(-29.04, -112.54) * mm, "end": v(-25.1, -111.97) * mm});
            skLineSegment(sketch, "E222.trimOffspring", {"start": v(-29.55, -111.8) * mm, "end": v(-25.68, -111.24) * mm});
            skLineSegment(sketch, "E223.trimOffspring", {"start": v(-25.68, -111.24) * mm, "end": v(-27.18, -109.36) * mm});
            skLineSegment(sketch, "E224.trimOffspring", {"start": v(-23.53, -111.74) * mm, "end": v(-19.64, -111.17) * mm});
            skLineSegment(sketch, "E225.trimOffspring", {"start": v(-23.53, -111.74) * mm, "end": v(-22.58, -112.95) * mm});
            skLineSegment(sketch, "E226.trimOffspring", {"start": v(-24.1, -111.01) * mm, "end": v(-20.22, -110.45) * mm});
            skLineSegment(sketch, "E227.trimOffspring", {"start": v(-25.61, -109.07) * mm, "end": v(-21.89, -108.38) * mm});
            skLineSegment(sketch, "E228.trimOffspring", {"start": v(-27.63, -108.8) * mm, "end": v(-28.53, -107.67) * mm});
            skLineSegment(sketch, "E229.trimOffspring", {"start": v(-26.07, -108.49) * mm, "end": v(-22.4, -107.76) * mm});
            skLineSegment(sketch, "E230.trimOffspring", {"start": v(-25.61, -109.07) * mm, "end": v(-24.1, -111.01) * mm});
            skLineSegment(sketch, "E231.trimOffspring", {"start": v(-22.12, -105.73) * mm, "end": v(-20.75, -107.43) * mm});
            skLineSegment(sketch, "E232.trimOffspring", {"start": v(-22.12, -105.73) * mm, "end": v(-17.27, -104.68) * mm});
            skLineSegment(sketch, "E233.trimOffspring", {"start": v(-20.75, -107.43) * mm, "end": v(-16.22, -106.54) * mm});
            skLineSegment(sketch, "E234.trimOffspring", {"start": v(-22.4, -107.76) * mm, "end": v(-24.64, -104.97) * mm});
            skLineSegment(sketch, "E235.trimOffspring", {"start": v(-20.23, -108.08) * mm, "end": v(-18.51, -110.2) * mm});
            skLineSegment(sketch, "E236.trimOffspring", {"start": v(-18.51, -110.2) * mm, "end": v(-14.5, -109.62) * mm});
            skLineSegment(sketch, "E237.trimOffspring", {"start": v(-17.93, -110.92) * mm, "end": v(-14.07, -110.36) * mm});
            skLineSegment(sketch, "E238.trimOffspring", {"start": v(-22.58, -112.95) * mm, "end": v(-18.56, -112.5) * mm});
            skLineSegment(sketch, "E239.trimOffspring", {"start": v(-24.18, -113.13) * mm, "end": v(-25.1, -111.97) * mm});
            skLineSegment(sketch, "E240.trimOffspring", {"start": v(-22.1, -113.57) * mm, "end": v(-21.69, -114.1) * mm});
            skLineSegment(sketch, "E241.trimOffspring", {"start": v(-28.3, -113.6) * mm, "end": v(-24.18, -113.13) * mm});
            skLineSegment(sketch, "E242.trimOffspring", {"start": v(-18.56, -112.5) * mm, "end": v(-21.89, -108.38) * mm});
            skLineSegment(sketch, "E243.trimOffspring", {"start": v(-16.81, -112.3) * mm, "end": v(-13.2, -111.9) * mm});
            skLineSegment(sketch, "E244.trimOffspring", {"start": v(-16.25, -113) * mm, "end": v(-12.78, -112.66) * mm});
            skLineSegment(sketch, "E245.trimOffspring", {"start": v(-16.25, -113) * mm, "end": v(-15.38, -114.07) * mm});
            skLineSegment(sketch, "E246.trimOffspring", {"start": v(-12.78, -112.66) * mm, "end": v(-12, -114.06) * mm});
            skLineSegment(sketch, "E247.trimOffspring", {"start": v(-11.63, -111.73) * mm, "end": v(-6.24, -111.12) * mm});
            skLineSegment(sketch, "E248.trimOffspring", {"start": v(-11.23, -112.5) * mm, "end": v(-10.43, -114.05) * mm});
            skLineSegment(sketch, "E249", {"start": v(-22.1, -113.57) * mm, "end": v(-18.03, -113.17) * mm});
            skLineSegment(sketch, "E250.trimOffspring", {"start": v(-14.07, -110.36) * mm, "end": v(-13.2, -111.9) * mm});
            skLineSegment(sketch, "E251.trimOffspring", {"start": v(-12.46, -110.13) * mm, "end": v(-7.31, -109.38) * mm});
            skLineSegment(sketch, "E252.trimOffspring", {"start": v(-12.46, -110.13) * mm, "end": v(-11.63, -111.73) * mm});
            skLineSegment(sketch, "E253.trimOffspring", {"start": v(-12.85, -109.38) * mm, "end": v(-7.77, -108.64) * mm});
            skLineSegment(sketch, "E254.trimOffspring", {"start": v(-14.11, -106.95) * mm, "end": v(-9.35, -106.08) * mm});
            skLineSegment(sketch, "E255.trimOffspring", {"start": v(-14.5, -106.2) * mm, "end": v(-9.85, -105.27) * mm});
            skLineSegment(sketch, "E256.trimOffspring", {"start": v(-14.11, -106.95) * mm, "end": v(-12.85, -109.38) * mm});
            skLineSegment(sketch, "E257", {"start": v(-20.23, -108.08) * mm, "end": v(-15.94, -107.37) * mm});
            skLineSegment(sketch, "E258", {"start": v(-15.94, -107.37) * mm, "end": v(-14.5, -109.62) * mm});
            skLineSegment(sketch, "E259.trimOffspring", {"start": v(-17.93, -110.92) * mm, "end": v(-16.81, -112.3) * mm});
            skLineSegment(sketch, "E260.trimOffspring", {"start": v(-15.49, -104.3) * mm, "end": v(-11.04, -103.35) * mm});
            skLineSegment(sketch, "E261.trimOffspring", {"start": v(-17.27, -104.68) * mm, "end": v(-16.22, -106.54) * mm});
            skLineSegment(sketch, "E262.trimOffspring", {"start": v(-16.1, -103.13) * mm, "end": v(-11.75, -102.2) * mm});
            skLineSegment(sketch, "E263.trimOffspring", {"start": v(-15.49, -104.3) * mm, "end": v(-14.5, -106.2) * mm});
            skLineSegment(sketch, "E264.trimOffspring", {"start": v(-13.68, -99.08) * mm, "end": v(-14.43, -97.86) * mm});
            skLineSegment(sketch, "E265.trimOffspring", {"start": v(-10.5, -99.03) * mm, "end": v(-6.74, -98.1) * mm});
            skLineSegment(sketch, "E266.trimOffspring", {"start": v(-10.91, -98.35) * mm, "end": v(-7.14, -97.37) * mm});
            skLineSegment(sketch, "E267.trimOffspring", {"start": v(-10.5, -99.03) * mm, "end": v(-8.92, -101.58) * mm});
            skLineSegment(sketch, "E268.trimOffspring", {"start": v(-11.75, -102.2) * mm, "end": v(-13.28, -99.72) * mm});
            skLineSegment(sketch, "E269.trimOffspring", {"start": v(-8.2, -102.74) * mm, "end": v(-4.63, -101.97) * mm});
            skLineSegment(sketch, "E270.trimOffspring", {"start": v(-8.92, -101.58) * mm, "end": v(-5.27, -100.8) * mm});
            skLineSegment(sketch, "E271.trimOffspring", {"start": v(-8.2, -102.74) * mm, "end": v(-7, -104.7) * mm});
            skLineSegment(sketch, "E272.trimOffspring", {"start": v(-7, -104.7) * mm, "end": v(-3.51, -104.01) * mm});
            skLineSegment(sketch, "E273.trimOffspring", {"start": v(-9.85, -105.27) * mm, "end": v(-11.04, -103.35) * mm});
            skLineSegment(sketch, "E274.trimOffspring", {"start": v(-6.47, -105.55) * mm, "end": v(-3.02, -104.91) * mm});
            skLineSegment(sketch, "E275.trimOffspring", {"start": v(-6.47, -105.55) * mm, "end": v(-4.82, -108.21) * mm});
            skLineSegment(sketch, "E276.trimOffspring", {"start": v(-7.77, -108.64) * mm, "end": v(-9.35, -106.08) * mm});
            skLineSegment(sketch, "E277.trimOffspring", {"start": v(-4.82, -108.21) * mm, "end": v(-1.49, -107.73) * mm});
            skLineSegment(sketch, "E278.trimOffspring", {"start": v(-4.37, -108.95) * mm, "end": v(-1.08, -108.48) * mm});
            skLineSegment(sketch, "E279.trimOffspring", {"start": v(-4.37, -108.95) * mm, "end": v(-3.23, -110.78) * mm});
            skLineSegment(sketch, "E280.trimOffspring", {"start": v(-3.23, -110.78) * mm, "end": v(-0.02, -110.42) * mm});
            skLineSegment(sketch, "E281.trimOffspring", {"start": v(-6.24, -111.12) * mm, "end": v(-7.31, -109.38) * mm});
            skLineSegment(sketch, "E282.trimOffspring", {"start": v(-2.68, -111.67) * mm, "end": v(0.5, -111.36) * mm});
            skLineSegment(sketch, "E283.trimOffspring", {"start": v(-2.68, -111.67) * mm, "end": v(-1.74, -113.2) * mm});
            skLineSegment(sketch, "E284.trimOffspring", {"start": v(-1.74, -113.2) * mm, "end": v(1.34, -112.9) * mm});
            skLineSegment(sketch, "E285", {"start": v(-11.23, -112.5) * mm, "end": v(-5.71, -111.97) * mm});
            skLineSegment(sketch, "E286.trimOffspring", {"start": v(-7.84, -96.08) * mm, "end": v(-7.14, -97.37) * mm});
            skLineSegment(sketch, "E287.trimOffspring", {"start": v(-6, -94.53) * mm, "end": v(-2.67, -93.58) * mm});
            skLineSegment(sketch, "E288.trimOffspring", {"start": v(-6, -94.53) * mm, "end": v(-6.66, -93.35) * mm});
            skLineSegment(sketch, "E289.trimOffspring", {"start": v(-4.76, -96.75) * mm, "end": v(-1.44, -95.89) * mm});
            skLineSegment(sketch, "E290.trimOffspring", {"start": v(-6.74, -98.1) * mm, "end": v(-5.27, -100.8) * mm});
            skLineSegment(sketch, "E291.trimOffspring", {"start": v(-4.33, -97.5) * mm, "end": v(-1.02, -96.68) * mm});
            skLineSegment(sketch, "E292.trimOffspring", {"start": v(-4.76, -96.75) * mm, "end": v(-5.49, -95.45) * mm});
            skLineSegment(sketch, "E293.trimOffspring", {"start": v(-2.79, -100.26) * mm, "end": v(0.52, -99.55) * mm});
            skLineSegment(sketch, "E294.trimOffspring", {"start": v(-2.79, -100.26) * mm, "end": v(-4.33, -97.5) * mm});
            skLineSegment(sketch, "E295.trimOffspring", {"start": v(-2.13, -101.43) * mm, "end": v(1.15, -100.73) * mm});
            skLineSegment(sketch, "E296.trimOffspring", {"start": v(-4.63, -101.97) * mm, "end": v(-3.51, -104.01) * mm});
            skLineSegment(sketch, "E297.trimOffspring", {"start": v(-0.97, -103.5) * mm, "end": v(2.3, -102.86) * mm});
            skLineSegment(sketch, "E298.trimOffspring", {"start": v(-3.02, -104.91) * mm, "end": v(-1.49, -107.73) * mm});
            skLineSegment(sketch, "E299.trimOffspring", {"start": v(-0.45, -104.44) * mm, "end": v(2.82, -103.84) * mm});
            skLineSegment(sketch, "E300.trimOffspring", {"start": v(-0.97, -103.5) * mm, "end": v(-2.13, -101.43) * mm});
            skLineSegment(sketch, "E301.trimOffspring", {"start": v(1.18, -107.34) * mm, "end": v(4.44, -106.87) * mm});
            skLineSegment(sketch, "E302.trimOffspring", {"start": v(-1.08, -108.48) * mm, "end": v(-0.02, -110.42) * mm});
            skLineSegment(sketch, "E303.trimOffspring", {"start": v(1.6, -108.09) * mm, "end": v(4.85, -107.62) * mm});
            skLineSegment(sketch, "E304.trimOffspring", {"start": v(1.18, -107.34) * mm, "end": v(-0.45, -104.44) * mm});
            skLineSegment(sketch, "E305.trimOffspring", {"start": v(2.74, -110.11) * mm, "end": v(5.99, -109.75) * mm});
            skLineSegment(sketch, "E306.trimOffspring", {"start": v(0.5, -111.36) * mm, "end": v(1.34, -112.9) * mm});
            skLineSegment(sketch, "E307.trimOffspring", {"start": v(3.28, -111.09) * mm, "end": v(6.54, -110.77) * mm});
            skLineSegment(sketch, "E308.trimOffspring", {"start": v(2.74, -110.11) * mm, "end": v(1.6, -108.09) * mm});
            skLineSegment(sketch, "E309.trimOffspring", {"start": v(4.14, -112.63) * mm, "end": v(7.36, -112.31) * mm});
            skLineSegment(sketch, "E310.trimOffspring", {"start": v(1.78, -113.7) * mm, "end": v(1.93, -113.99) * mm});
            skLineSegment(sketch, "E311.trimOffspring", {"start": v(4.14, -112.63) * mm, "end": v(3.28, -111.09) * mm});
            skLineSegment(sketch, "E312.trimOffspring", {"start": v(7.8, -113.12) * mm, "end": v(8.24, -113.96) * mm});
            skLineSegment(sketch, "E313.trimOffspring", {"start": v(10.36, -112.87) * mm, "end": v(12.94, -112.62) * mm});
            skLineSegment(sketch, "E314.trimOffspring", {"start": v(9.93, -112.06) * mm, "end": v(9.1, -110.52) * mm});
            skLineSegment(sketch, "E315.trimOffspring", {"start": v(9.93, -112.06) * mm, "end": v(12.52, -111.8) * mm});
            skLineSegment(sketch, "E316", {"start": v(4.6, -113.43) * mm, "end": v(7.8, -113.12) * mm});
            skLineSegment(sketch, "E317.trimOffspring", {"start": v(9.1, -110.52) * mm, "end": v(11.71, -110.27) * mm});
            skLineSegment(sketch, "E318.trimOffspring", {"start": v(6.54, -110.77) * mm, "end": v(7.36, -112.31) * mm});
            skLineSegment(sketch, "E319.trimOffspring", {"start": v(8.53, -109.46) * mm, "end": v(11.14, -109.17) * mm});
            skLineSegment(sketch, "E320.trimOffspring", {"start": v(8.53, -109.46) * mm, "end": v(7.35, -107.25) * mm});
            skLineSegment(sketch, "E321.trimOffspring", {"start": v(7.35, -107.25) * mm, "end": v(9.94, -106.88) * mm});
            skLineSegment(sketch, "E322.trimOffspring", {"start": v(4.85, -107.62) * mm, "end": v(5.99, -109.75) * mm});
            skLineSegment(sketch, "E323.trimOffspring", {"start": v(6.95, -106.5) * mm, "end": v(9.55, -106.12) * mm});
            skLineSegment(sketch, "E324.trimOffspring", {"start": v(6.95, -106.5) * mm, "end": v(5.28, -103.39) * mm});
            skLineSegment(sketch, "E325.trimOffspring", {"start": v(5.28, -103.39) * mm, "end": v(7.87, -102.9) * mm});
            skLineSegment(sketch, "E326.trimOffspring", {"start": v(2.82, -103.84) * mm, "end": v(4.44, -106.87) * mm});
            skLineSegment(sketch, "E327.trimOffspring", {"start": v(4.74, -102.38) * mm, "end": v(7.33, -101.86) * mm});
            skLineSegment(sketch, "E328.trimOffspring", {"start": v(4.74, -102.38) * mm, "end": v(3.57, -100.2) * mm});
            skLineSegment(sketch, "E329.trimOffspring", {"start": v(3.57, -100.2) * mm, "end": v(6.17, -99.65) * mm});
            skLineSegment(sketch, "E330.trimOffspring", {"start": v(1.15, -100.73) * mm, "end": v(2.3, -102.86) * mm});
            skLineSegment(sketch, "E331.trimOffspring", {"start": v(2.94, -99.03) * mm, "end": v(1.37, -96.09) * mm});
            skLineSegment(sketch, "E332.trimOffspring", {"start": v(2.94, -99.03) * mm, "end": v(5.56, -98.47) * mm});
            skLineSegment(sketch, "E333.trimOffspring", {"start": v(1.37, -96.09) * mm, "end": v(3.98, -95.44) * mm});
            skLineSegment(sketch, "E334.trimOffspring", {"start": v(-1.02, -96.68) * mm, "end": v(0.52, -99.55) * mm});
            skLineSegment(sketch, "E335.trimOffspring", {"start": v(0.93, -95.27) * mm, "end": v(0.2, -93.91) * mm});
            skLineSegment(sketch, "E336.trimOffspring", {"start": v(0.93, -95.27) * mm, "end": v(3.53, -94.6) * mm});
            skLineSegment(sketch, "E337.trimOffspring", {"start": v(0.2, -93.91) * mm, "end": v(2.8, -93.2) * mm});
            skLineSegment(sketch, "E338.trimOffspring", {"start": v(-0.33, -92.92) * mm, "end": v(-1.03, -91.6) * mm});
            skLineSegment(sketch, "E339.trimOffspring", {"start": v(-0.33, -92.92) * mm, "end": v(2.27, -92.17) * mm});
            skLineSegment(sketch, "E340", {"start": v(-5.49, -95.45) * mm, "end": v(-2.15, -94.54) * mm});
            skLineSegment(sketch, "E341", {"start": v(-2.15, -94.54) * mm, "end": v(-1.44, -95.89) * mm});
            skLineSegment(sketch, "E342.trimOffspring", {"start": v(-1.03, -91.6) * mm, "end": v(1.56, -90.8) * mm});
            skLineSegment(sketch, "E343.trimOffspring", {"start": v(-3.35, -92.32) * mm, "end": v(-2.67, -93.58) * mm});
            skLineSegment(sketch, "E344.trimOffspring", {"start": v(-1.42, -90.89) * mm, "end": v(1.16, -90.04) * mm});
            skLineSegment(sketch, "E345.trimOffspring", {"start": v(-1.42, -90.89) * mm, "end": v(-2.23, -89.38) * mm});
            skLineSegment(sketch, "E346.trimOffspring", {"start": v(1.56, -90.8) * mm, "end": v(2.27, -92.17) * mm});
            skLineSegment(sketch, "E347.trimOffspring", {"start": v(3.03, -89.43) * mm, "end": v(5.81, -88.53) * mm});
            skLineSegment(sketch, "E348.trimOffspring", {"start": v(2, -87.4) * mm, "end": v(4.88, -86.57) * mm});
            skLineSegment(sketch, "E349.trimOffspring", {"start": v(3.43, -90.23) * mm, "end": v(6.21, -89.37) * mm});
            skLineSegment(sketch, "E350.trimOffspring", {"start": v(4.14, -91.64) * mm, "end": v(6.91, -90.85) * mm});
            skLineSegment(sketch, "E351.trimOffspring", {"start": v(2.8, -93.2) * mm, "end": v(3.53, -94.6) * mm});
            skLineSegment(sketch, "E352.trimOffspring", {"start": v(4.14, -91.64) * mm, "end": v(3.43, -90.23) * mm});
            skLineSegment(sketch, "E353.trimOffspring", {"start": v(4.68, -92.7) * mm, "end": v(7.44, -91.95) * mm});
            skLineSegment(sketch, "E354.trimOffspring", {"start": v(5.39, -94.1) * mm, "end": v(8.13, -93.4) * mm});
            skLineSegment(sketch, "E355.trimOffspring", {"start": v(5.39, -94.1) * mm, "end": v(4.68, -92.7) * mm});
            skLineSegment(sketch, "E356.trimOffspring", {"start": v(3.98, -95.44) * mm, "end": v(5.56, -98.47) * mm});
            skLineSegment(sketch, "E357.trimOffspring", {"start": v(5.83, -94.98) * mm, "end": v(8.56, -94.3) * mm});
            skLineSegment(sketch, "E358.trimOffspring", {"start": v(7.39, -98.07) * mm, "end": v(10.08, -97.5) * mm});
            skLineSegment(sketch, "E359.trimOffspring", {"start": v(6.17, -99.65) * mm, "end": v(7.33, -101.86) * mm});
            skLineSegment(sketch, "E360.trimOffspring", {"start": v(7.39, -98.07) * mm, "end": v(5.83, -94.98) * mm});
            skLineSegment(sketch, "E361.trimOffspring", {"start": v(7.99, -99.26) * mm, "end": v(10.65, -98.69) * mm});
            skLineSegment(sketch, "E362.trimOffspring", {"start": v(9.12, -101.5) * mm, "end": v(11.74, -100.99) * mm});
            skLineSegment(sketch, "E363.trimOffspring", {"start": v(7.87, -102.9) * mm, "end": v(9.55, -106.12) * mm});
            skLineSegment(sketch, "E364.trimOffspring", {"start": v(9.12, -101.5) * mm, "end": v(7.99, -99.26) * mm});
            skLineSegment(sketch, "E365.trimOffspring", {"start": v(9.66, -102.58) * mm, "end": v(12.27, -102.1) * mm});
            skLineSegment(sketch, "E366.trimOffspring", {"start": v(11.32, -105.87) * mm, "end": v(13.89, -105.5) * mm});
            skLineSegment(sketch, "E367.trimOffspring", {"start": v(9.94, -106.88) * mm, "end": v(11.14, -109.17) * mm});
            skLineSegment(sketch, "E368.trimOffspring", {"start": v(11.7, -106.62) * mm, "end": v(14.25, -106.25) * mm});
            skLineSegment(sketch, "E369.trimOffspring", {"start": v(11.32, -105.87) * mm, "end": v(9.66, -102.58) * mm});
            skLineSegment(sketch, "E370.trimOffspring", {"start": v(12.9, -108.97) * mm, "end": v(15.41, -108.7) * mm});
            skLineSegment(sketch, "E371.trimOffspring", {"start": v(11.71, -110.27) * mm, "end": v(12.52, -111.8) * mm});
            skLineSegment(sketch, "E372.trimOffspring", {"start": v(13.46, -110.1) * mm, "end": v(15.96, -109.85) * mm});
            skLineSegment(sketch, "E373.trimOffspring", {"start": v(12.9, -108.97) * mm, "end": v(11.7, -106.62) * mm});
            skLineSegment(sketch, "E374.trimOffspring", {"start": v(14.24, -111.64) * mm, "end": v(16.7, -111.4) * mm});
            skLineSegment(sketch, "E375.trimOffspring", {"start": v(12.94, -112.62) * mm, "end": v(13.63, -113.93) * mm});
            skLineSegment(sketch, "E376.trimOffspring", {"start": v(14.65, -112.45) * mm, "end": v(17.09, -112.21) * mm});
            skLineSegment(sketch, "E377.trimOffspring", {"start": v(14.24, -111.64) * mm, "end": v(13.46, -110.1) * mm});
            skLineSegment(sketch, "E378.trimOffspring", {"start": v(19.78, -113.18) * mm, "end": v(22.03, -112.91) * mm});
            skLineSegment(sketch, "E379.trimOffspring", {"start": v(17.09, -112.21) * mm, "end": v(17.9, -113.9) * mm});
            skLineSegment(sketch, "E380.trimOffspring", {"start": v(18.81, -111.2) * mm, "end": v(18.06, -109.65) * mm});
            skLineSegment(sketch, "E381.trimOffspring", {"start": v(18.81, -111.2) * mm, "end": v(21.2, -110.96) * mm});
            skLineSegment(sketch, "E382.trimOffspring", {"start": v(15.96, -109.85) * mm, "end": v(16.7, -111.4) * mm});
            skLineSegment(sketch, "E383.trimOffspring", {"start": v(18.06, -109.65) * mm, "end": v(20.55, -109.4) * mm});
            skLineSegment(sketch, "E384.trimOffspring", {"start": v(17.49, -108.46) * mm, "end": v(16.27, -105.96) * mm});
            skLineSegment(sketch, "E385.trimOffspring", {"start": v(17.49, -108.46) * mm, "end": v(20.03, -108.17) * mm});
            skLineSegment(sketch, "E386.trimOffspring", {"start": v(16.27, -105.96) * mm, "end": v(18.92, -105.57) * mm});
            skLineSegment(sketch, "E387.trimOffspring", {"start": v(14.25, -106.25) * mm, "end": v(15.41, -108.7) * mm});
            skLineSegment(sketch, "E388.trimOffspring", {"start": v(15.9, -105.2) * mm, "end": v(14.23, -101.74) * mm});
            skLineSegment(sketch, "E389.trimOffspring", {"start": v(15.9, -105.2) * mm, "end": v(18.6, -104.8) * mm});
            skLineSegment(sketch, "E390.trimOffspring", {"start": v(14.23, -101.74) * mm, "end": v(17.07, -101.21) * mm});
            skLineSegment(sketch, "E391.trimOffspring", {"start": v(12.27, -102.1) * mm, "end": v(13.89, -105.5) * mm});
            skLineSegment(sketch, "E392.trimOffspring", {"start": v(13.68, -100.6) * mm, "end": v(12.55, -98.28) * mm});
            skLineSegment(sketch, "E393.trimOffspring", {"start": v(13.68, -100.6) * mm, "end": v(16.57, -100.03) * mm});
            skLineSegment(sketch, "E394.trimOffspring", {"start": v(12.55, -98.28) * mm, "end": v(15.56, -97.63) * mm});
            skLineSegment(sketch, "E395.trimOffspring", {"start": v(10.65, -98.69) * mm, "end": v(11.74, -100.99) * mm});
            skLineSegment(sketch, "E396.trimOffspring", {"start": v(11.97, -97.08) * mm, "end": v(10.4, -93.84) * mm});
            skLineSegment(sketch, "E397.trimOffspring", {"start": v(11.97, -97.08) * mm, "end": v(15.04, -96.42) * mm});
            skLineSegment(sketch, "E398.trimOffspring", {"start": v(10.4, -93.84) * mm, "end": v(13.61, -93.05) * mm});
            skLineSegment(sketch, "E399.trimOffspring", {"start": v(8.56, -94.3) * mm, "end": v(10.08, -97.5) * mm});
            skLineSegment(sketch, "E400.trimOffspring", {"start": v(9.95, -92.92) * mm, "end": v(9.25, -91.46) * mm});
            skLineSegment(sketch, "E401.trimOffspring", {"start": v(9.95, -92.92) * mm, "end": v(13.2, -92.07) * mm});
            skLineSegment(sketch, "E402.trimOffspring", {"start": v(9.25, -91.46) * mm, "end": v(12.56, -90.57) * mm});
            skLineSegment(sketch, "E403.trimOffspring", {"start": v(7.44, -91.95) * mm, "end": v(8.13, -93.4) * mm});
            skLineSegment(sketch, "E404.trimOffspring", {"start": v(8.7, -90.33) * mm, "end": v(7.97, -88.83) * mm});
            skLineSegment(sketch, "E405.trimOffspring", {"start": v(7.97, -88.83) * mm, "end": v(11.38, -87.78) * mm});
            skLineSegment(sketch, "E406.trimOffspring", {"start": v(6.21, -89.37) * mm, "end": v(6.91, -90.85) * mm});
            skLineSegment(sketch, "E407.trimOffspring", {"start": v(3.03, -89.43) * mm, "end": v(2, -87.4) * mm});
            skLineSegment(sketch, "E408.trimOffspring", {"start": v(7.55, -87.96) * mm, "end": v(6.63, -86.07) * mm});
            skLineSegment(sketch, "E409.trimOffspring", {"start": v(7.55, -87.96) * mm, "end": v(10.98, -86.84) * mm});
            skLineSegment(sketch, "E410.trimOffspring", {"start": v(6.63, -86.07) * mm, "end": v(10.22, -85.05) * mm});
            skLineSegment(sketch, "E411.trimOffspring", {"start": v(4.88, -86.57) * mm, "end": v(5.81, -88.53) * mm});
            skLineSegment(sketch, "E412.trimOffspring", {"start": v(6.25, -85.28) * mm, "end": v(5.6, -83.93) * mm});
            skLineSegment(sketch, "E413.trimOffspring", {"start": v(6.25, -85.28) * mm, "end": v(9.86, -84.2) * mm});
            skLineSegment(sketch, "E414.trimOffspring", {"start": v(10.22, -85.05) * mm, "end": v(10.98, -86.84) * mm});
            skLineSegment(sketch, "E415.trimOffspring", {"start": v(12.06, -83.52) * mm, "end": v(10.7, -80.38) * mm});
            skLineSegment(sketch, "E416.trimOffspring", {"start": v(12.06, -83.52) * mm, "end": v(15.49, -82.49) * mm});
            skLineSegment(sketch, "E417.trimOffspring", {"start": v(12.44, -84.41) * mm, "end": v(15.82, -83.45) * mm});
            skLineSegment(sketch, "E418.trimOffspring", {"start": v(13.18, -86.13) * mm, "end": v(16.38, -85.08) * mm});
            skLineSegment(sketch, "E419.trimOffspring", {"start": v(12.56, -90.57) * mm, "end": v(13.2, -92.07) * mm});
            skLineSegment(sketch, "E420.trimOffspring", {"start": v(13.6, -87.1) * mm, "end": v(16.74, -86.12) * mm});
            skLineSegment(sketch, "E421.trimOffspring", {"start": v(13.18, -86.13) * mm, "end": v(12.44, -84.41) * mm});
            skLineSegment(sketch, "E422.trimOffspring", {"start": v(14.3, -88.73) * mm, "end": v(17.33, -87.87) * mm});
            skLineSegment(sketch, "E423.trimOffspring", {"start": v(14.83, -89.96) * mm, "end": v(17.78, -89.16) * mm});
            skLineSegment(sketch, "E424.trimOffspring", {"start": v(14.3, -88.73) * mm, "end": v(13.6, -87.1) * mm});
            skLineSegment(sketch, "E425.trimOffspring", {"start": v(15.49, -91.48) * mm, "end": v(18.32, -90.74) * mm});
            skLineSegment(sketch, "E426.trimOffspring", {"start": v(13.61, -93.05) * mm, "end": v(15.04, -96.42) * mm});
            skLineSegment(sketch, "E427.trimOffspring", {"start": v(15.92, -92.47) * mm, "end": v(18.68, -91.79) * mm});
            skLineSegment(sketch, "E428.trimOffspring", {"start": v(15.49, -91.48) * mm, "end": v(14.83, -89.96) * mm});
            skLineSegment(sketch, "E429", {"start": v(8.7, -90.33) * mm, "end": v(12.04, -89.43) * mm});
            skLineSegment(sketch, "E430", {"start": v(12.04, -89.43) * mm, "end": v(11.38, -87.78) * mm});
            skLineSegment(sketch, "E431.trimOffspring", {"start": v(17.4, -95.92) * mm, "end": v(19.9, -95.38) * mm});
            skLineSegment(sketch, "E432.trimOffspring", {"start": v(15.56, -97.63) * mm, "end": v(16.57, -100.03) * mm});
            skLineSegment(sketch, "E433.trimOffspring", {"start": v(17.92, -97.12) * mm, "end": v(20.33, -96.6) * mm});
            skLineSegment(sketch, "E434.trimOffspring", {"start": v(17.4, -95.92) * mm, "end": v(15.92, -92.47) * mm});
            skLineSegment(sketch, "E435.trimOffspring", {"start": v(18.97, -99.55) * mm, "end": v(21.2, -99.11) * mm});
            skLineSegment(sketch, "E436.trimOffspring", {"start": v(17.07, -101.21) * mm, "end": v(18.6, -104.8) * mm});
            skLineSegment(sketch, "E437.trimOffspring", {"start": v(18.97, -99.55) * mm, "end": v(17.92, -97.12) * mm});
            skLineSegment(sketch, "E438.trimOffspring", {"start": v(21.08, -104.45) * mm, "end": v(22.93, -104.18) * mm});
            skLineSegment(sketch, "E439.trimOffspring", {"start": v(18.92, -105.57) * mm, "end": v(20.03, -108.17) * mm});
            skLineSegment(sketch, "E440.trimOffspring", {"start": v(21.4, -105.21) * mm, "end": v(23.2, -104.95) * mm});
            skLineSegment(sketch, "E441.trimOffspring", {"start": v(21.08, -104.45) * mm, "end": v(19.5, -100.77) * mm});
            skLineSegment(sketch, "E442.trimOffspring", {"start": v(22.56, -107.89) * mm, "end": v(24.14, -107.71) * mm});
            skLineSegment(sketch, "E443.trimOffspring", {"start": v(20.55, -109.4) * mm, "end": v(21.2, -110.96) * mm});
            skLineSegment(sketch, "E444.trimOffspring", {"start": v(23.1, -109.15) * mm, "end": v(24.59, -109) * mm});
            skLineSegment(sketch, "E445.trimOffspring", {"start": v(22.56, -107.89) * mm, "end": v(21.4, -105.21) * mm});
            skLineSegment(sketch, "E446.trimOffspring", {"start": v(23.77, -110.7) * mm, "end": v(25.12, -110.58) * mm});
            skLineSegment(sketch, "E447.trimOffspring", {"start": v(21.55, -111.78) * mm, "end": v(22.03, -112.91) * mm});
            skLineSegment(sketch, "E448.trimOffspring", {"start": v(24.13, -111.52) * mm, "end": v(25.4, -111.4) * mm});
            skLineSegment(sketch, "E449.trimOffspring", {"start": v(23.77, -110.7) * mm, "end": v(23.1, -109.15) * mm});
            skLineSegment(sketch, "E450.trimOffspring", {"start": v(24.6, -112.6) * mm, "end": v(25.77, -112.46) * mm});
            skLineSegment(sketch, "E451.trimOffspring", {"start": v(22.34, -113.63) * mm, "end": v(22.45, -113.88) * mm});
            skLineSegment(sketch, "E452.trimOffspring", {"start": v(24.9, -113.32) * mm, "end": v(26.02, -113.18) * mm});
            skLineSegment(sketch, "E453", {"start": v(19.2, -112) * mm, "end": v(21.55, -111.78) * mm});
            skLineSegment(sketch, "E454.trimOffspring", {"start": v(24.6, -112.6) * mm, "end": v(24.13, -111.52) * mm});
            skLineSegment(sketch, "E455.trimOffspring", {"start": v(25.77, -112.46) * mm, "end": v(25.4, -111.4) * mm});
            skLineSegment(sketch, "E456.trimOffspring", {"start": v(27.38, -113.02) * mm, "end": v(28.88, -112.84) * mm});
            skLineSegment(sketch, "E457.trimOffspring", {"start": v(27.38, -113.02) * mm, "end": v(27.64, -113.86) * mm});
            skLineSegment(sketch, "E458.trimOffspring", {"start": v(27.16, -112.3) * mm, "end": v(28.79, -112.1) * mm});
            skLineSegment(sketch, "E459.trimOffspring", {"start": v(26.84, -111.26) * mm, "end": v(28.67, -111.08) * mm});
            skLineSegment(sketch, "E460.trimOffspring", {"start": v(25.12, -110.58) * mm, "end": v(24.59, -109) * mm});
            skLineSegment(sketch, "E461.trimOffspring", {"start": v(26.59, -110.43) * mm, "end": v(28.57, -110.24) * mm});
            skLineSegment(sketch, "E462.trimOffspring", {"start": v(26.84, -111.26) * mm, "end": v(27.16, -112.3) * mm});
            skLineSegment(sketch, "E463.trimOffspring", {"start": v(26.1, -108.86) * mm, "end": v(28.37, -108.64) * mm});
            skLineSegment(sketch, "E464.trimOffspring", {"start": v(24.14, -107.71) * mm, "end": v(23.2, -104.95) * mm});
            skLineSegment(sketch, "E465.trimOffspring", {"start": v(26.1, -108.86) * mm, "end": v(26.59, -110.43) * mm});
            skLineSegment(sketch, "E466.trimOffspring", {"start": v(25.7, -107.54) * mm, "end": v(28.2, -107.26) * mm});
            skLineSegment(sketch, "E467.trimOffspring", {"start": v(24.82, -104.71) * mm, "end": v(27.84, -104.28) * mm});
            skLineSegment(sketch, "E468.trimOffspring", {"start": v(21.2, -99.11) * mm, "end": v(20.33, -96.6) * mm});
            skLineSegment(sketch, "E469.trimOffspring", {"start": v(24.82, -104.71) * mm, "end": v(25.7, -107.54) * mm});
            skLineSegment(sketch, "E470.trimOffspring", {"start": v(24.58, -103.94) * mm, "end": v(27.28, -103.55) * mm});
            skLineSegment(sketch, "E471.trimOffspring", {"start": v(23.38, -100.05) * mm, "end": v(26.53, -99.47) * mm});
            skLineSegment(sketch, "E472.trimOffspring", {"start": v(22.98, -98.76) * mm, "end": v(26.13, -98.13) * mm});
            skLineSegment(sketch, "E473.trimOffspring", {"start": v(23.38, -100.05) * mm, "end": v(24.58, -103.94) * mm});
            skLineSegment(sketch, "E474.trimOffspring", {"start": v(24.96, -94.29) * mm, "end": v(23.82, -90.51) * mm});
            skLineSegment(sketch, "E475", {"start": v(19.5, -100.77) * mm, "end": v(21.5, -100.34) * mm});
            skLineSegment(sketch, "E476", {"start": v(21.5, -100.34) * mm, "end": v(22.93, -104.18) * mm});
            skLineSegment(sketch, "E477.trimOffspring", {"start": v(19.9, -95.38) * mm, "end": v(18.68, -91.79) * mm});
            skLineSegment(sketch, "E478.trimOffspring", {"start": v(21.81, -94.97) * mm, "end": v(24.96, -94.29) * mm});
            skLineSegment(sketch, "E479.trimOffspring", {"start": v(22.2, -96.2) * mm, "end": v(22.98, -98.76) * mm});
            skPoint(sketch, "E480.orphan", {"position": v(26.75, -95.23) * mm});
            skLineSegment(sketch, "E481", {"start": v(22.2, -96.2) * mm, "end": v(25.1, -95.58) * mm});
            skLineSegment(sketch, "E482", {"start": v(25.1, -95.58) * mm, "end": v(26.13, -98.13) * mm});
            skLineSegment(sketch, "E483.trimOffspring", {"start": v(20.68, -91.3) * mm, "end": v(23.82, -90.51) * mm});
            skLineSegment(sketch, "E484.trimOffspring", {"start": v(18.32, -90.74) * mm, "end": v(17.78, -89.16) * mm});
            skLineSegment(sketch, "E485.trimOffspring", {"start": v(20.68, -91.3) * mm, "end": v(21.9, -95.23) * mm});
            skLineSegment(sketch, "E486.trimOffspring", {"start": v(20.34, -90.21) * mm, "end": v(23.48, -89.4) * mm});
            skLineSegment(sketch, "E487.trimOffspring", {"start": v(19.85, -88.6) * mm, "end": v(22.98, -87.75) * mm});
            skLineSegment(sketch, "E488.trimOffspring", {"start": v(17.33, -87.87) * mm, "end": v(16.74, -86.12) * mm});
            skLineSegment(sketch, "E489.trimOffspring", {"start": v(19.85, -88.6) * mm, "end": v(20.34, -90.21) * mm});
            skLineSegment(sketch, "E490.trimOffspring", {"start": v(19.44, -87.27) * mm, "end": v(22.56, -86.38) * mm});
            skLineSegment(sketch, "E491.trimOffspring", {"start": v(18.88, -85.46) * mm, "end": v(22, -84.5) * mm});
            skLineSegment(sketch, "E492.trimOffspring", {"start": v(16.38, -85.08) * mm, "end": v(15.82, -83.45) * mm});
            skLineSegment(sketch, "E493.trimOffspring", {"start": v(18.88, -85.46) * mm, "end": v(19.44, -87.27) * mm});
            skLineSegment(sketch, "E494.trimOffspring", {"start": v(18.54, -84.38) * mm, "end": v(21.65, -83.37) * mm});
            skLineSegment(sketch, "E495.trimOffspring", {"start": v(15.49, -82.49) * mm, "end": v(13.98, -78.1) * mm});
            skLineSegment(sketch, "E496.trimOffspring", {"start": v(18.06, -82.8) * mm, "end": v(18.54, -84.38) * mm});
            skLineSegment(sketch, "E497.trimOffspring", {"start": v(17.75, -81.8) * mm, "end": v(20.89, -80.85) * mm});
            skLineSegment(sketch, "E498.trimOffspring", {"start": v(22.16, -80.46) * mm, "end": v(24.87, -79.64) * mm});
            skLineSegment(sketch, "E499.trimOffspring", {"start": v(20.89, -80.85) * mm, "end": v(19, -74.6) * mm});
            skLineSegment(sketch, "E500.trimOffspring", {"start": v(22.52, -81.54) * mm, "end": v(25, -80.83) * mm});
            skLineSegment(sketch, "E501.trimOffspring", {"start": v(22.98, -82.94) * mm, "end": v(25.18, -82.22) * mm});
            skLineSegment(sketch, "E502.trimOffspring", {"start": v(21.65, -83.37) * mm, "end": v(21.2, -81.91) * mm});
            skLineSegment(sketch, "E503.trimOffspring", {"start": v(23.35, -84.08) * mm, "end": v(25.33, -83.47) * mm});
            skLineSegment(sketch, "E504.trimOffspring", {"start": v(23.35, -84.08) * mm, "end": v(23.98, -85.97) * mm});
            skLineSegment(sketch, "E505", {"start": v(18.06, -82.8) * mm, "end": v(21.2, -81.91) * mm});
            skLineSegment(sketch, "E506", {"start": v(22.52, -81.54) * mm, "end": v(22.98, -82.94) * mm});
            skLineSegment(sketch, "E507.trimOffspring", {"start": v(23.98, -85.97) * mm, "end": v(25.58, -85.51) * mm});
            skLineSegment(sketch, "E508.trimOffspring", {"start": v(22.56, -86.38) * mm, "end": v(22, -84.5) * mm});
            skLineSegment(sketch, "E509.trimOffspring", {"start": v(24.43, -87.36) * mm, "end": v(25.76, -87) * mm});
            skLineSegment(sketch, "E510.trimOffspring", {"start": v(24.43, -87.36) * mm, "end": v(24.97, -89) * mm});
            skLineSegment(sketch, "E511.trimOffspring", {"start": v(24.97, -89) * mm, "end": v(25.97, -88.75) * mm});
            skLineSegment(sketch, "E512.trimOffspring", {"start": v(23.48, -89.4) * mm, "end": v(22.98, -87.75) * mm});
            skLineSegment(sketch, "E513.trimOffspring", {"start": v(25.34, -90.13) * mm, "end": v(26.11, -89.94) * mm});
            skLineSegment(sketch, "E514.trimOffspring", {"start": v(25.34, -90.13) * mm, "end": v(26.6, -93.94) * mm});
            skLineSegment(sketch, "E515", {"start": v(26.53, -99.47) * mm, "end": v(27.28, -103.55) * mm});
            skSolve(sketch);
        }
        {
            var Q0;
            Q0=makeQuery(id+"F15.imprint","IMPRINT",FACE,{"disambiguationData":[TD([[makeQuery(id+"F15.imprint","IMPRINT",EDGE,{"derivedFrom":sQuery(id+"F15.wireOp",EDGE,"E166")}),-1.0]])]});
            var Q1;
            {var subQ0=sQuery(id+"F15.wireOp",EDGE,"E173");Q1=makeQuery(id+"F15.imprint","IMPRINT",FACE,{"disambiguationData":[TD([[makeQuery(id+"F15.imprint","IMPRINT",EDGE,{"derivedFrom":subQ0}),1.0]])]});}
            var Q2;
            {var subQ2=sQuery(id+"F15.wireOp",EDGE,"E198");Q2=makeQuery(id+"F15.imprint","IMPRINT",FACE,{"disambiguationData":[TD([[makeQuery(id+"F15.imprint","IMPRINT",EDGE,{"derivedFrom":subQ2}),1.0]])]});}
            var Q3;
            Q3=makeQuery(id+"F15.imprint","IMPRINT",FACE,{"disambiguationData":[TD([[makeQuery(id+"F15.imprint","IMPRINT",EDGE,{"derivedFrom":sQuery(id+"F15.wireOp",EDGE,"E175")}),1.0]])]});
            var Q4;
            {var subQ0=sQuery(id+"F15.wireOp",EDGE,"E205");Q4=makeQuery(id+"F15.imprint","IMPRINT",FACE,{"disambiguationData":[TD([[makeQuery(id+"F15.imprint","IMPRINT",EDGE,{"derivedFrom":subQ0}),1.0]])]});}
            var Q5;
            Q5=makeQuery(id+"F15.imprint","IMPRINT",FACE,{"disambiguationData":[TD([[makeQuery(id+"F15.imprint","IMPRINT",EDGE,{"derivedFrom":sQuery(id+"F15.wireOp",EDGE,"E220.trimOffspring")}),1.0]])]});
            var Q6;
            {var subQ0=sQuery(id+"F15.wireOp",EDGE,"E176");Q6=makeQuery(id+"F15.imprint","IMPRINT",FACE,{"disambiguationData":[TD([[makeQuery(id+"F15.imprint","IMPRINT",EDGE,{"derivedFrom":subQ0}),1.0]])]});}
            var Q7;
            {var subQ0=sQuery(id+"F15.wireOp",EDGE,"E178");Q7=makeQuery(id+"F15.imprint","IMPRINT",FACE,{"disambiguationData":[TD([[makeQuery(id+"F15.imprint","IMPRINT",EDGE,{"derivedFrom":subQ0}),1.0]])]});}
            var Q8;
            {var subQ0=sQuery(id+"F15.wireOp",EDGE,"E224.trimOffspring");Q8=makeQuery(id+"F15.imprint","IMPRINT",FACE,{"disambiguationData":[TD([[makeQuery(id+"F15.imprint","IMPRINT",EDGE,{"derivedFrom":subQ0}),-1.0]])]});}
            var Q9;
            {var subQ0=sQuery(id+"F15.wireOp",EDGE,"E226.trimOffspring");Q9=makeQuery(id+"F15.imprint","IMPRINT",FACE,{"disambiguationData":[TD([[makeQuery(id+"F15.imprint","IMPRINT",EDGE,{"derivedFrom":subQ0}),1.0]])]});}
            var Q10;
            {var subQ0=sQuery(id+"F15.wireOp",EDGE,"E177");Q10=makeQuery(id+"F15.imprint","IMPRINT",FACE,{"disambiguationData":[TD([[makeQuery(id+"F15.imprint","IMPRINT",EDGE,{"derivedFrom":subQ0}),1.0]])]});}
            var Q11;
            {var subQ0=sQuery(id+"F15.wireOp",EDGE,"E179");Q11=makeQuery(id+"F15.imprint","IMPRINT",FACE,{"disambiguationData":[TD([[makeQuery(id+"F15.imprint","IMPRINT",EDGE,{"derivedFrom":subQ0}),1.0]])]});}
            var Q12;
            Q12=makeQuery(id+"F15.imprint","IMPRINT",FACE,{"disambiguationData":[TD([[makeQuery(id+"F15.imprint","IMPRINT",EDGE,{"derivedFrom":sQuery(id+"F15.wireOp",EDGE,"E231.trimOffspring")}),1.0]])]});
            var Q13;
            Q13=makeQuery(id+"F15.imprint","IMPRINT",FACE,{"disambiguationData":[TD([[makeQuery(id+"F15.imprint","IMPRINT",EDGE,{"derivedFrom":sQuery(id+"F15.wireOp",EDGE,"E235.trimOffspring")}),1.0]])]});
            var Q14;
            Q14=makeQuery(id+"F15.imprint","IMPRINT",FACE,{"disambiguationData":[TD([[makeQuery(id+"F15.imprint","IMPRINT",EDGE,{"derivedFrom":sQuery(id+"F15.wireOp",EDGE,"E237.trimOffspring")}),-1.0]])]});
            var Q15;
            Q15=makeQuery(id+"F15.imprint","IMPRINT",FACE,{"disambiguationData":[TD([[makeQuery(id+"F15.imprint","IMPRINT",EDGE,{"derivedFrom":sQuery(id+"F15.wireOp",EDGE,"E244.trimOffspring")}),-1.0]])]});
            var Q16;
            {var subQ0=sQuery(id+"F15.wireOp",EDGE,"E182");Q16=makeQuery(id+"F15.imprint","IMPRINT",FACE,{"disambiguationData":[TD([[makeQuery(id+"F15.imprint","IMPRINT",EDGE,{"derivedFrom":subQ0}),1.0]])]});}
            var Q17;
            Q17=makeQuery(id+"F15.imprint","IMPRINT",FACE,{"disambiguationData":[TD([[makeQuery(id+"F15.imprint","IMPRINT",EDGE,{"derivedFrom":sQuery(id+"F15.wireOp",EDGE,"E247.trimOffspring")}),1.0]])]});
            var Q18;
            Q18=makeQuery(id+"F15.imprint","IMPRINT",FACE,{"disambiguationData":[TD([[makeQuery(id+"F15.imprint","IMPRINT",EDGE,{"derivedFrom":sQuery(id+"F15.wireOp",EDGE,"E253.trimOffspring")}),1.0]])]});
            var Q19;
            Q19=makeQuery(id+"F15.imprint","IMPRINT",FACE,{"disambiguationData":[TD([[makeQuery(id+"F15.imprint","IMPRINT",EDGE,{"derivedFrom":sQuery(id+"F15.wireOp",EDGE,"E255.trimOffspring")}),1.0]])]});
            var Q20;
            Q20=makeQuery(id+"F15.imprint","IMPRINT",FACE,{"disambiguationData":[TD([[makeQuery(id+"F15.imprint","IMPRINT",EDGE,{"derivedFrom":sQuery(id+"F15.wireOp",EDGE,"E181")}),1.0]])]});
            var Q21;
            {var subQ0=sQuery(id+"F15.wireOp",EDGE,"E209");Q21=makeQuery(id+"F15.imprint","IMPRINT",FACE,{"disambiguationData":[TD([[makeQuery(id+"F15.imprint","IMPRINT",EDGE,{"derivedFrom":subQ0}),1.0]])]});}
            var Q22;
            {var subQ0=sQuery(id+"F15.wireOp",EDGE,"E184");Q22=makeQuery(id+"F15.imprint","IMPRINT",FACE,{"disambiguationData":[TD([[makeQuery(id+"F15.imprint","IMPRINT",EDGE,{"derivedFrom":subQ0}),-1.0]])]});}
            var Q23;
            Q23=makeQuery(id+"F15.imprint","IMPRINT",FACE,{"disambiguationData":[TD([[makeQuery(id+"F15.imprint","IMPRINT",EDGE,{"derivedFrom":sQuery(id+"F15.wireOp",EDGE,"E183")}),1.0]])]});
            var Q24;
            Q24=makeQuery(id+"F15.imprint","IMPRINT",FACE,{"disambiguationData":[TD([[makeQuery(id+"F15.imprint","IMPRINT",EDGE,{"derivedFrom":sQuery(id+"F15.wireOp",EDGE,"E265.trimOffspring")}),-1.0]])]});
            var Q25;
            Q25=makeQuery(id+"F15.imprint","IMPRINT",FACE,{"disambiguationData":[TD([[makeQuery(id+"F15.imprint","IMPRINT",EDGE,{"derivedFrom":sQuery(id+"F15.wireOp",EDGE,"E269.trimOffspring")}),-1.0]])]});
            var Q26;
            Q26=makeQuery(id+"F15.imprint","IMPRINT",FACE,{"disambiguationData":[TD([[makeQuery(id+"F15.imprint","IMPRINT",EDGE,{"derivedFrom":sQuery(id+"F15.wireOp",EDGE,"E274.trimOffspring")}),-1.0]])]});
            var Q27;
            Q27=makeQuery(id+"F15.imprint","IMPRINT",FACE,{"disambiguationData":[TD([[makeQuery(id+"F15.imprint","IMPRINT",EDGE,{"derivedFrom":sQuery(id+"F15.wireOp",EDGE,"E278.trimOffspring")}),-1.0]])]});
            var Q28;
            Q28=makeQuery(id+"F15.imprint","IMPRINT",FACE,{"disambiguationData":[TD([[makeQuery(id+"F15.imprint","IMPRINT",EDGE,{"derivedFrom":sQuery(id+"F15.wireOp",EDGE,"E282.trimOffspring")}),-1.0]])]});
            var Q29;
            {var subQ0=sQuery(id+"F15.wireOp",EDGE,"E185");Q29=makeQuery(id+"F15.imprint","IMPRINT",FACE,{"disambiguationData":[TD([[makeQuery(id+"F15.imprint","IMPRINT",EDGE,{"derivedFrom":subQ0}),-1.0]])]});}
            var Q30;
            Q30=makeQuery(id+"F15.imprint","IMPRINT",FACE,{"disambiguationData":[TD([[makeQuery(id+"F15.imprint","IMPRINT",EDGE,{"derivedFrom":sQuery(id+"F15.wireOp",EDGE,"E307.trimOffspring")}),-1.0]])]});
            var Q31;
            Q31=makeQuery(id+"F15.imprint","IMPRINT",FACE,{"disambiguationData":[TD([[makeQuery(id+"F15.imprint","IMPRINT",EDGE,{"derivedFrom":sQuery(id+"F15.wireOp",EDGE,"E303.trimOffspring")}),-1.0]])]});
            var Q32;
            Q32=makeQuery(id+"F15.imprint","IMPRINT",FACE,{"disambiguationData":[TD([[makeQuery(id+"F15.imprint","IMPRINT",EDGE,{"derivedFrom":sQuery(id+"F15.wireOp",EDGE,"E299.trimOffspring")}),-1.0]])]});
            var Q33;
            Q33=makeQuery(id+"F15.imprint","IMPRINT",FACE,{"disambiguationData":[TD([[makeQuery(id+"F15.imprint","IMPRINT",EDGE,{"derivedFrom":sQuery(id+"F15.wireOp",EDGE,"E295.trimOffspring")}),-1.0]])]});
            var Q34;
            {var subQ0=sQuery(id+"F15.wireOp",EDGE,"E200");Q34=makeQuery(id+"F15.imprint","IMPRINT",FACE,{"disambiguationData":[TD([[makeQuery(id+"F15.imprint","IMPRINT",EDGE,{"derivedFrom":subQ0}),-1.0]])]});}
            var Q35;
            Q35=makeQuery(id+"F15.imprint","IMPRINT",FACE,{"disambiguationData":[TD([[makeQuery(id+"F15.imprint","IMPRINT",EDGE,{"derivedFrom":sQuery(id+"F15.wireOp",EDGE,"E291.trimOffspring")}),-1.0]])]});
            var Q36;
            Q36=makeQuery(id+"F15.imprint","IMPRINT",FACE,{"disambiguationData":[TD([[makeQuery(id+"F15.imprint","IMPRINT",EDGE,{"derivedFrom":sQuery(id+"F15.wireOp",EDGE,"E289.trimOffspring")}),1.0]])]});
            var Q37;
            Q37=makeQuery(id+"F15.imprint","IMPRINT",FACE,{"disambiguationData":[TD([[makeQuery(id+"F15.imprint","IMPRINT",EDGE,{"derivedFrom":sQuery(id+"F15.wireOp",EDGE,"E212")}),-1.0]])]});
            var Q38;
            {var subQ0=sQuery(id+"F15.wireOp",EDGE,"E186");Q38=makeQuery(id+"F15.imprint","IMPRINT",FACE,{"disambiguationData":[TD([[makeQuery(id+"F15.imprint","IMPRINT",EDGE,{"derivedFrom":subQ0}),-1.0]])]});}
            var Q39;
            {var subQ0=sQuery(id+"F15.wireOp",EDGE,"E188");Q39=makeQuery(id+"F15.imprint","IMPRINT",FACE,{"disambiguationData":[TD([[makeQuery(id+"F15.imprint","IMPRINT",EDGE,{"derivedFrom":subQ0}),-1.0]])]});}
            var Q40;
            Q40=makeQuery(id+"F15.imprint","IMPRINT",FACE,{"disambiguationData":[TD([[makeQuery(id+"F15.imprint","IMPRINT",EDGE,{"derivedFrom":sQuery(id+"F15.wireOp",EDGE,"E338.trimOffspring")}),-1.0]])]});
            var Q41;
            Q41=makeQuery(id+"F15.imprint","IMPRINT",FACE,{"disambiguationData":[TD([[makeQuery(id+"F15.imprint","IMPRINT",EDGE,{"derivedFrom":sQuery(id+"F15.wireOp",EDGE,"E335.trimOffspring")}),-1.0]])]});
            var Q42;
            Q42=makeQuery(id+"F15.imprint","IMPRINT",FACE,{"disambiguationData":[TD([[makeQuery(id+"F15.imprint","IMPRINT",EDGE,{"derivedFrom":sQuery(id+"F15.wireOp",EDGE,"E331.trimOffspring")}),-1.0]])]});
            var Q43;
            Q43=makeQuery(id+"F15.imprint","IMPRINT",FACE,{"disambiguationData":[TD([[makeQuery(id+"F15.imprint","IMPRINT",EDGE,{"derivedFrom":sQuery(id+"F15.wireOp",EDGE,"E327.trimOffspring")}),1.0]])]});
            var Q44;
            Q44=makeQuery(id+"F15.imprint","IMPRINT",FACE,{"disambiguationData":[TD([[makeQuery(id+"F15.imprint","IMPRINT",EDGE,{"derivedFrom":sQuery(id+"F15.wireOp",EDGE,"E319.trimOffspring")}),1.0]])]});
            var Q45;
            Q45=makeQuery(id+"F15.imprint","IMPRINT",FACE,{"disambiguationData":[TD([[makeQuery(id+"F15.imprint","IMPRINT",EDGE,{"derivedFrom":sQuery(id+"F15.wireOp",EDGE,"E314.trimOffspring")}),-1.0]])]});
            var Q46;
            {var subQ0=sQuery(id+"F15.wireOp",EDGE,"E187");Q46=makeQuery(id+"F15.imprint","IMPRINT",FACE,{"disambiguationData":[TD([[makeQuery(id+"F15.imprint","IMPRINT",EDGE,{"derivedFrom":subQ0}),-1.0]])]});}
            var Q47;
            Q47=makeQuery(id+"F15.imprint","IMPRINT",FACE,{"disambiguationData":[TD([[makeQuery(id+"F15.imprint","IMPRINT",EDGE,{"derivedFrom":sQuery(id+"F15.wireOp",EDGE,"E323.trimOffspring")}),1.0]])]});
            var Q48;
            {var subQ0=sQuery(id+"F15.wireOp",EDGE,"E189");Q48=makeQuery(id+"F15.imprint","IMPRINT",FACE,{"disambiguationData":[TD([[makeQuery(id+"F15.imprint","IMPRINT",EDGE,{"derivedFrom":subQ0}),-1.0]])]});}
            var Q49;
            Q49=makeQuery(id+"F15.imprint","IMPRINT",FACE,{"disambiguationData":[TD([[makeQuery(id+"F15.imprint","IMPRINT",EDGE,{"derivedFrom":sQuery(id+"F15.wireOp",EDGE,"E372.trimOffspring")}),-1.0]])]});
            var Q50;
            Q50=makeQuery(id+"F15.imprint","IMPRINT",FACE,{"disambiguationData":[TD([[makeQuery(id+"F15.imprint","IMPRINT",EDGE,{"derivedFrom":sQuery(id+"F15.wireOp",EDGE,"E368.trimOffspring")}),-1.0]])]});
            var Q51;
            Q51=makeQuery(id+"F15.imprint","IMPRINT",FACE,{"disambiguationData":[TD([[makeQuery(id+"F15.imprint","IMPRINT",EDGE,{"derivedFrom":sQuery(id+"F15.wireOp",EDGE,"E365.trimOffspring")}),-1.0]])]});
            var Q52;
            Q52=makeQuery(id+"F15.imprint","IMPRINT",FACE,{"disambiguationData":[TD([[makeQuery(id+"F15.imprint","IMPRINT",EDGE,{"derivedFrom":sQuery(id+"F15.wireOp",EDGE,"E361.trimOffspring")}),-1.0]])]});
            var Q53;
            Q53=makeQuery(id+"F15.imprint","IMPRINT",FACE,{"disambiguationData":[TD([[makeQuery(id+"F15.imprint","IMPRINT",EDGE,{"derivedFrom":sQuery(id+"F15.wireOp",EDGE,"E357.trimOffspring")}),-1.0]])]});
            var Q54;
            Q54=makeQuery(id+"F15.imprint","IMPRINT",FACE,{"disambiguationData":[TD([[makeQuery(id+"F15.imprint","IMPRINT",EDGE,{"derivedFrom":sQuery(id+"F15.wireOp",EDGE,"E353.trimOffspring")}),-1.0]])]});
            var Q55;
            Q55=makeQuery(id+"F15.imprint","IMPRINT",FACE,{"disambiguationData":[TD([[makeQuery(id+"F15.imprint","IMPRINT",EDGE,{"derivedFrom":sQuery(id+"F15.wireOp",EDGE,"E347.trimOffspring")}),1.0]])]});
            var Q56;
            {var subQ0=sQuery(id+"F15.wireOp",EDGE,"E190");Q56=makeQuery(id+"F15.imprint","IMPRINT",FACE,{"disambiguationData":[TD([[makeQuery(id+"F15.imprint","IMPRINT",EDGE,{"derivedFrom":subQ0}),-1.0]])]});}
            var Q57;
            {var subQ0=sQuery(id+"F15.wireOp",EDGE,"E192");Q57=makeQuery(id+"F15.imprint","IMPRINT",FACE,{"disambiguationData":[TD([[makeQuery(id+"F15.imprint","IMPRINT",EDGE,{"derivedFrom":subQ0}),-1.0]])]});}
            var Q58;
            Q58=makeQuery(id+"F15.imprint","IMPRINT",FACE,{"disambiguationData":[TD([[makeQuery(id+"F15.imprint","IMPRINT",EDGE,{"derivedFrom":sQuery(id+"F15.wireOp",EDGE,"E408.trimOffspring")}),-1.0]])]});
            var Q59;
            Q59=makeQuery(id+"F15.imprint","IMPRINT",FACE,{"disambiguationData":[TD([[makeQuery(id+"F15.imprint","IMPRINT",EDGE,{"derivedFrom":sQuery(id+"F15.wireOp",EDGE,"E404.trimOffspring")}),-1.0]])]});
            var Q60;
            Q60=makeQuery(id+"F15.imprint","IMPRINT",FACE,{"disambiguationData":[TD([[makeQuery(id+"F15.imprint","IMPRINT",EDGE,{"derivedFrom":sQuery(id+"F15.wireOp",EDGE,"E400.trimOffspring")}),-1.0]])]});
            var Q61;
            Q61=makeQuery(id+"F15.imprint","IMPRINT",FACE,{"disambiguationData":[TD([[makeQuery(id+"F15.imprint","IMPRINT",EDGE,{"derivedFrom":sQuery(id+"F15.wireOp",EDGE,"E396.trimOffspring")}),-1.0]])]});
            var Q62;
            Q62=makeQuery(id+"F15.imprint","IMPRINT",FACE,{"disambiguationData":[TD([[makeQuery(id+"F15.imprint","IMPRINT",EDGE,{"derivedFrom":sQuery(id+"F15.wireOp",EDGE,"E392.trimOffspring")}),-1.0]])]});
            var Q63;
            Q63=makeQuery(id+"F15.imprint","IMPRINT",FACE,{"disambiguationData":[TD([[makeQuery(id+"F15.imprint","IMPRINT",EDGE,{"derivedFrom":sQuery(id+"F15.wireOp",EDGE,"E388.trimOffspring")}),-1.0]])]});
            var Q64;
            Q64=makeQuery(id+"F15.imprint","IMPRINT",FACE,{"disambiguationData":[TD([[makeQuery(id+"F15.imprint","IMPRINT",EDGE,{"derivedFrom":sQuery(id+"F15.wireOp",EDGE,"E384.trimOffspring")}),-1.0]])]});
            var Q65;
            Q65=makeQuery(id+"F15.imprint","IMPRINT",FACE,{"disambiguationData":[TD([[makeQuery(id+"F15.imprint","IMPRINT",EDGE,{"derivedFrom":sQuery(id+"F15.wireOp",EDGE,"E380.trimOffspring")}),-1.0]])]});
            var Q66;
            Q66=makeQuery(id+"F15.imprint","IMPRINT",FACE,{"disambiguationData":[TD([[makeQuery(id+"F15.imprint","IMPRINT",EDGE,{"derivedFrom":sQuery(id+"F15.wireOp",EDGE,"E191")}),-1.0]])]});
            var Q67;
            Q67=makeQuery(id+"F15.imprint","IMPRINT",FACE,{"disambiguationData":[TD([[makeQuery(id+"F15.imprint","IMPRINT",EDGE,{"derivedFrom":sQuery(id+"F15.wireOp",EDGE,"E349.trimOffspring")}),-1.0]])]});
            var Q68;
            {var subQ0=sQuery(id+"F15.wireOp",EDGE,"E415.trimOffspring");Q68=makeQuery(id+"F15.imprint","IMPRINT",FACE,{"disambiguationData":[TD([[makeQuery(id+"F15.imprint","IMPRINT",EDGE,{"derivedFrom":subQ0}),-1.0]])]});}
            var Q69;
            Q69=makeQuery(id+"F15.imprint","IMPRINT",FACE,{"disambiguationData":[TD([[makeQuery(id+"F15.imprint","IMPRINT",EDGE,{"derivedFrom":sQuery(id+"F15.wireOp",EDGE,"E417.trimOffspring")}),-1.0]])]});
            var Q70;
            {var subQ0=sQuery(id+"F15.wireOp",EDGE,"E195");Q70=makeQuery(id+"F15.imprint","IMPRINT",FACE,{"disambiguationData":[TD([[makeQuery(id+"F15.imprint","IMPRINT",EDGE,{"derivedFrom":subQ0}),1.0]])]});}
            var Q71;
            Q71=makeQuery(id+"F15.imprint","IMPRINT",FACE,{"disambiguationData":[TD([[makeQuery(id+"F15.imprint","IMPRINT",EDGE,{"derivedFrom":sQuery(id+"F15.wireOp",EDGE,"E196")}),1.0]])]});
            var Q72;
            {var subQ0=sQuery(id+"F15.wireOp",EDGE,"E500.trimOffspring");Q72=makeQuery(id+"F15.imprint","IMPRINT",FACE,{"disambiguationData":[TD([[makeQuery(id+"F15.imprint","IMPRINT",EDGE,{"derivedFrom":subQ0}),-1.0]])]});}
            var Q73;
            Q73=makeQuery(id+"F15.imprint","IMPRINT",FACE,{"disambiguationData":[TD([[makeQuery(id+"F15.imprint","IMPRINT",EDGE,{"derivedFrom":sQuery(id+"F15.wireOp",EDGE,"E494.trimOffspring")}),1.0]])]});
            var Q74;
            Q74=makeQuery(id+"F15.imprint","IMPRINT",FACE,{"disambiguationData":[TD([[makeQuery(id+"F15.imprint","IMPRINT",EDGE,{"derivedFrom":sQuery(id+"F15.wireOp",EDGE,"E490.trimOffspring")}),1.0]])]});
            var Q75;
            Q75=makeQuery(id+"F15.imprint","IMPRINT",FACE,{"disambiguationData":[TD([[makeQuery(id+"F15.imprint","IMPRINT",EDGE,{"derivedFrom":sQuery(id+"F15.wireOp",EDGE,"E420.trimOffspring")}),-1.0]])]});
            var Q76;
            Q76=makeQuery(id+"F15.imprint","IMPRINT",FACE,{"disambiguationData":[TD([[makeQuery(id+"F15.imprint","IMPRINT",EDGE,{"derivedFrom":sQuery(id+"F15.wireOp",EDGE,"E423.trimOffspring")}),-1.0]])]});
            var Q77;
            {var subQ0=sQuery(id+"F15.wireOp",EDGE,"E503.trimOffspring");Q77=makeQuery(id+"F15.imprint","IMPRINT",FACE,{"disambiguationData":[TD([[makeQuery(id+"F15.imprint","IMPRINT",EDGE,{"derivedFrom":subQ0}),-1.0]])]});}
            var Q78;
            {var subQ0=sQuery(id+"F15.wireOp",EDGE,"E509.trimOffspring");Q78=makeQuery(id+"F15.imprint","IMPRINT",FACE,{"disambiguationData":[TD([[makeQuery(id+"F15.imprint","IMPRINT",EDGE,{"derivedFrom":subQ0}),-1.0]])]});}
            var Q79;
            Q79=makeQuery(id+"F15.imprint","IMPRINT",FACE,{"disambiguationData":[TD([[makeQuery(id+"F15.imprint","IMPRINT",EDGE,{"derivedFrom":sQuery(id+"F15.wireOp",EDGE,"E486.trimOffspring")}),1.0]])]});
            var Q80;
            Q80=makeQuery(id+"F15.imprint","IMPRINT",FACE,{"disambiguationData":[TD([[makeQuery(id+"F15.imprint","IMPRINT",EDGE,{"derivedFrom":sQuery(id+"F15.wireOp",EDGE,"E474.trimOffspring")}),1.0]])]});
            var Q81;
            {var subQ0=sQuery(id+"F15.wireOp",EDGE,"E513.trimOffspring");Q81=makeQuery(id+"F15.imprint","IMPRINT",FACE,{"disambiguationData":[TD([[makeQuery(id+"F15.imprint","IMPRINT",EDGE,{"derivedFrom":subQ0}),-1.0]])]});}
            var Q82;
            Q82=makeQuery(id+"F15.imprint","IMPRINT",FACE,{"disambiguationData":[TD([[makeQuery(id+"F15.imprint","IMPRINT",EDGE,{"derivedFrom":sQuery(id+"F15.wireOp",EDGE,"E427.trimOffspring")}),-1.0]])]});
            var Q83;
            Q83=makeQuery(id+"F15.imprint","IMPRINT",FACE,{"disambiguationData":[TD([[makeQuery(id+"F15.imprint","IMPRINT",EDGE,{"derivedFrom":sQuery(id+"F15.wireOp",EDGE,"E433.trimOffspring")}),-1.0]])]});
            var Q84;
            Q84=makeQuery(id+"F15.imprint","IMPRINT",FACE,{"disambiguationData":[TD([[makeQuery(id+"F15.imprint","IMPRINT",EDGE,{"derivedFrom":sQuery(id+"F15.wireOp",EDGE,"E472.trimOffspring")}),1.0]])]});
            var Q85;
            Q85=makeQuery(id+"F15.imprint","IMPRINT",FACE,{"disambiguationData":[TD([[makeQuery(id+"F15.imprint","IMPRINT",EDGE,{"derivedFrom":sQuery(id+"F15.wireOp",EDGE,"E438.trimOffspring")}),1.0]])]});
            var Q86;
            {var subQ0=sQuery(id+"F15.wireOp",EDGE,"E466.trimOffspring");Q86=makeQuery(id+"F15.imprint","IMPRINT",FACE,{"disambiguationData":[TD([[makeQuery(id+"F15.imprint","IMPRINT",EDGE,{"derivedFrom":subQ0}),1.0]])]});}
            var Q87;
            Q87=makeQuery(id+"F15.imprint","IMPRINT",FACE,{"disambiguationData":[TD([[makeQuery(id+"F15.imprint","IMPRINT",EDGE,{"derivedFrom":sQuery(id+"F15.wireOp",EDGE,"E440.trimOffspring")}),-1.0]])]});
            var Q88;
            Q88=makeQuery(id+"F15.imprint","IMPRINT",FACE,{"disambiguationData":[TD([[makeQuery(id+"F15.imprint","IMPRINT",EDGE,{"derivedFrom":sQuery(id+"F15.wireOp",EDGE,"E444.trimOffspring")}),-1.0]])]});
            var Q89;
            {var subQ0=sQuery(id+"F15.wireOp",EDGE,"E461.trimOffspring");Q89=makeQuery(id+"F15.imprint","IMPRINT",FACE,{"disambiguationData":[TD([[makeQuery(id+"F15.imprint","IMPRINT",EDGE,{"derivedFrom":subQ0}),1.0]])]});}
            var Q90;
            {var subQ0=sQuery(id+"F15.wireOp",EDGE,"E458.trimOffspring");Q90=makeQuery(id+"F15.imprint","IMPRINT",FACE,{"disambiguationData":[TD([[makeQuery(id+"F15.imprint","IMPRINT",EDGE,{"derivedFrom":subQ0}),1.0]])]});}
            var Q91;
            Q91=makeQuery(id+"F15.imprint","IMPRINT",FACE,{"disambiguationData":[TD([[makeQuery(id+"F15.imprint","IMPRINT",EDGE,{"derivedFrom":sQuery(id+"F15.wireOp",EDGE,"E448.trimOffspring")}),-1.0]])]});
            var Q92;
            {var subQ0=sQuery(id+"F15.wireOp",EDGE,"E193");Q92=makeQuery(id+"F15.imprint","IMPRINT",FACE,{"disambiguationData":[TD([[makeQuery(id+"F15.imprint","IMPRINT",EDGE,{"derivedFrom":subQ0}),-1.0]])]});}
            var Q93;
            {var subQ3=sQuery(id+"F15.wireOp",EDGE,"E456.trimOffspring");Q93=makeQuery(id+"F15.imprint","IMPRINT",FACE,{"disambiguationData":[TD([[makeQuery(id+"F15.imprint","IMPRINT",EDGE,{"derivedFrom":subQ3}),-1.0]])]});}
            var Q94;
            {var subQ0=sQuery(id+"F15.wireOp",EDGE,"E201");Q94=makeQuery(id+"F15.imprint","IMPRINT",FACE,{"disambiguationData":[TD([[makeQuery(id+"F15.imprint","IMPRINT",EDGE,{"derivedFrom":subQ0}),-1.0]])]});}
            var Q95;
            {var subQ3=sQuery(id+"F15.wireOp",EDGE,"E216");Q95=makeQuery(id+"F15.imprint","IMPRINT",FACE,{"disambiguationData":[TD([[makeQuery(id+"F15.imprint","IMPRINT",EDGE,{"derivedFrom":subQ3}),1.0]])]});}
            var Q96;
            Q96=makeQuery(id+"F15.imprint","IMPRINT",FACE,{"disambiguationData":[TD([[makeQuery(id+"F15.imprint","IMPRINT",EDGE,{"derivedFrom":sQuery(id+"F15.wireOp",EDGE,"E470.trimOffspring")}),1.0]])]});
            extrude(context, id + "F16", {"entities" : qUnion([Q0, Q1, Q2, Q3, Q4, Q5, Q6, Q7, Q8, Q9, Q10, Q11, Q12, Q13, Q14, Q15, Q16, Q17, Q18, Q19, Q20, Q21, Q22, Q23, Q24, Q25, Q26, Q27, Q28, Q29, Q30, Q31, Q32, Q33, Q34, Q35, Q36, Q37, Q38, Q39, Q40, Q41, Q42, Q43, Q44, Q45, Q46, Q47, Q48, Q49, Q50, Q51, Q52, Q53, Q54, Q55, Q56, Q57, Q58, Q59, Q60, Q61, Q62, Q63, Q64, Q65, Q66, Q67, Q68, Q69, Q70, Q71, Q72, Q73, Q74, Q75, Q76, Q77, Q78, Q79, Q80, Q81, Q82, Q83, Q84, Q85, Q86, Q87, Q88, Q89, Q90, Q91, Q92, Q93, Q94, Q95, Q96]), "operationType" : NewBodyOperationType.REMOVE, "depth" : 25.4 * mm});
        }
    });
